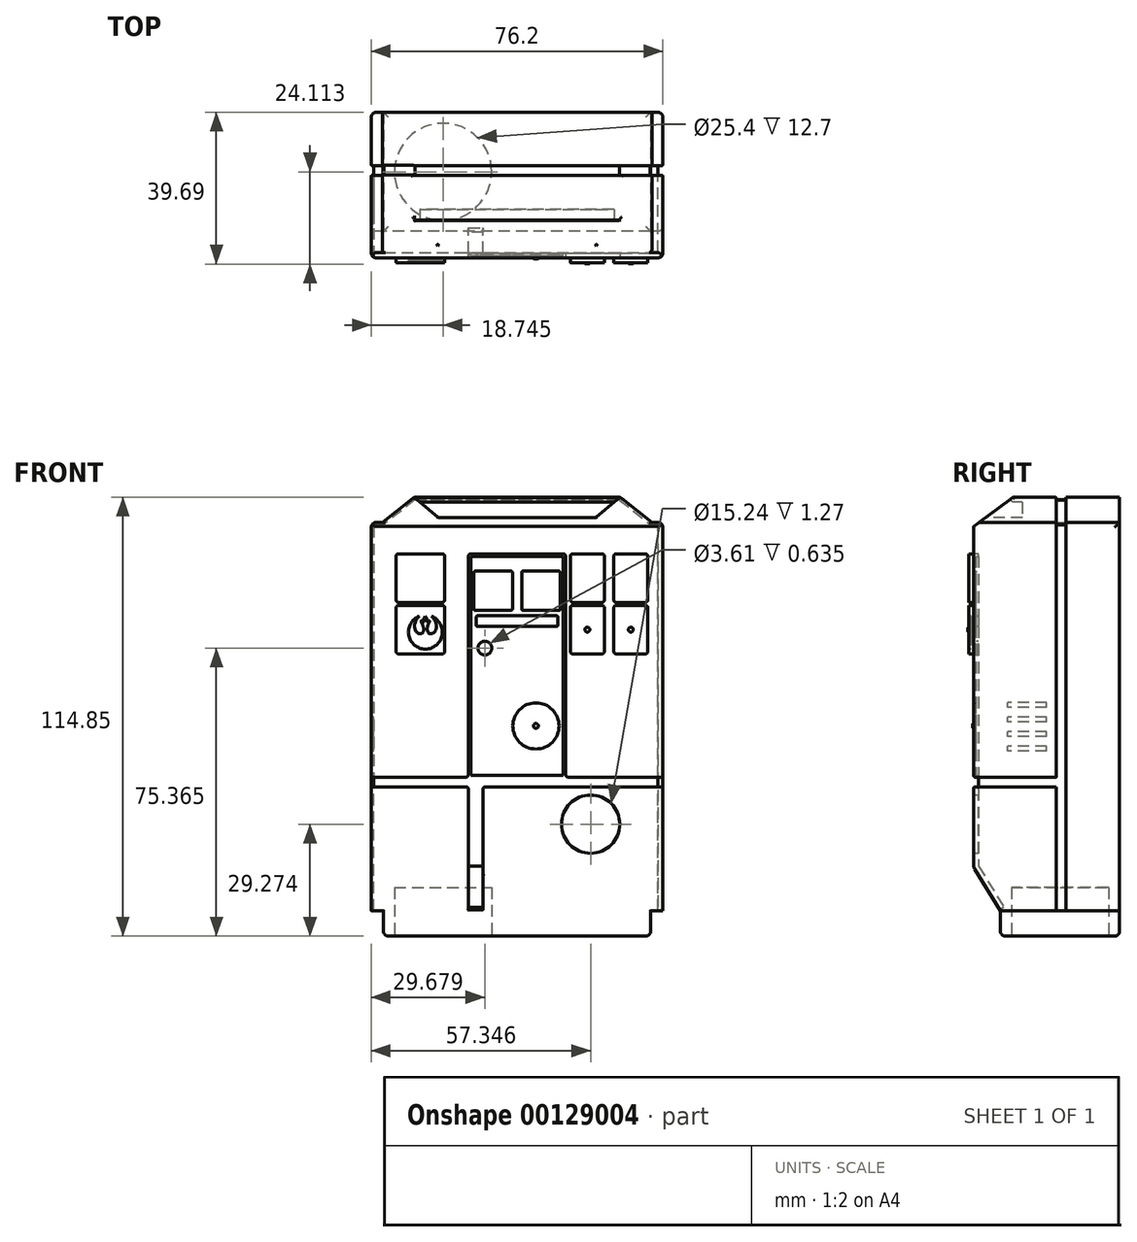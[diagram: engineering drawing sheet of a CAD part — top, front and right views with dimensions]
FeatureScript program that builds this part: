
annotation { "Feature Type Name" : "Feature", "Feature Type Description" : "" }
export const myFeature = defineFeature(function(context is Context, id is Id, definition is map)
    precondition{}
    {
        {
            var Q0;
            Q0=qCreatedBy(makeId("Right.planeOp"),FACE);
            var sketch = newSketch(context, id + "F0", { "sketchPlane" : qUnion([Q0])});
            skLineSegment(sketch, "E0.bottom", {"start": v(19.05, -50.8) * mm, "end": v(-12.1, -50.8) * mm});
            skLineSegment(sketch, "E0.top", {"start": v(19.05, 50.8) * mm, "end": v(-19.05, 50.8) * mm});
            skLineSegment(sketch, "E0.left", {"start": v(19.05, -50.8) * mm, "end": v(19.05, 50.8) * mm});
            skLineSegment(sketch, "E0.right", {"start": v(-19.05, -39.5) * mm, "end": v(-19.05, 50.8) * mm});
            skPoint(sketch, "E0.middle", {"position": v(0, 0) * mm});
            skLineSegment(sketch, "E1", {"start": v(-12.1, -50.8) * mm, "end": v(-19.05, -39.5) * mm});
            skPoint(sketch, "E2.orphan", {"position": v(-19.05, -50.8) * mm});
            skLineSegment(sketch, "E3.bottom", {"start": v(-12.1, -50.8) * mm, "end": v(19.05, -50.8) * mm});
            skLineSegment(sketch, "E3.top", {"start": v(-12.1, -57.41) * mm, "end": v(19.05, -57.41) * mm});
            skLineSegment(sketch, "E3.left", {"start": v(-12.1, -50.8) * mm, "end": v(-12.1, -57.41) * mm});
            skLineSegment(sketch, "E3.right", {"start": v(19.05, -50.8) * mm, "end": v(19.05, -57.41) * mm});
            skLineSegment(sketch, "E4", {"start": v(-44.45, -55.13) * mm, "end": v(6.35, -23.88) * mm, "construction": true});
            skSolve(sketch);
        }
        {
            var Q0;
            Q0=makeQuery(id+"F0.imprint","IMPRINT",FACE,{"disambiguationData":[TD([[makeQuery(id+"F0.imprint","IMPRINT",EDGE,{"derivedFrom":sQuery(id+"F0.wireOp",EDGE,"E0.top")}),1.0]])]});
            extrude(context, id + "F1", {"entities" : qUnion([Q0]), "endBound" : BoundingType.SYMMETRIC, "depth" : 76.2 * mm});
        }
        {
            var Q0;
            Q0 = qSketchRegion(id + "F0", true);
            extrude(context, id + "F2", {"entities" : qUnion([Q0]), "operationType" : NewBodyOperationType.ADD, "endBound" : BoundingType.SYMMETRIC, "depth" : 69.85 * mm});
        }
        {
            var Q0;
            Q0=makeQuery(id+"F1.opExtrude","SWEPT_EDGE",EDGE,{"disambiguationData":[OSD([sQuery(id+"F0.wireOp",EDGE,"E0.right"),sQuery(id+"F0.wireOp",EDGE,"E1")])]});
            var Q1;
            Q1=makeQuery(id+"F1.opExtrude","CAP_EDGE",EDGE,{"disambiguationData":[OSD([sQuery(id+"F0.wireOp",EDGE,"E1")])],"isStart":false});
            var Q2;
            Q2=makeQuery(id+"F1.opExtrude","CAP_EDGE",EDGE,{"disambiguationData":[OSD([sQuery(id+"F0.wireOp",EDGE,"E1")])],"isStart":true});
            var Q3;
            Q3=makeQuery(id+"F1.opExtrude","CAP_EDGE",EDGE,{"disambiguationData":[OSD([sQuery(id+"F0.wireOp",EDGE,"E0.right")])],"isStart":false});
            var Q4;
            Q4=makeQuery(id+"F1.opExtrude","SWEPT_EDGE",EDGE,{"disambiguationData":[OSD([sQuery(id+"F0.wireOp",EDGE,"E0.top"),sQuery(id+"F0.wireOp",EDGE,"E0.right")])]});
            var Q5;
            Q5=makeQuery(id+"F1.opExtrude","CAP_EDGE",EDGE,{"disambiguationData":[OSD([sQuery(id+"F0.wireOp",EDGE,"E0.right")])],"isStart":true});
            var Q6;
            Q6=makeQuery(id+"F1.opExtrude","CAP_EDGE",EDGE,{"disambiguationData":[OSD([sQuery(id+"F0.wireOp",EDGE,"E3.bottom")])],"isStart":true});
            var Q7;
            Q7=makeQuery(id+"F1.opExtrude","CAP_EDGE",EDGE,{"disambiguationData":[OSD([sQuery(id+"F0.wireOp",EDGE,"E3.bottom")])],"isStart":false});
            var Q8;
            Q8=makeQuery(id+"F1.opExtrude","CAP_EDGE",EDGE,{"disambiguationData":[OSD([sQuery(id+"F0.wireOp",EDGE,"E0.top")])],"isStart":false});
            var Q9;
            Q9=makeQuery(id+"F1.opExtrude","CAP_EDGE",EDGE,{"disambiguationData":[OSD([sQuery(id+"F0.wireOp",EDGE,"E0.left")])],"isStart":false});
            var Q10;
            Q10=makeQuery(id+"F1.opExtrude","CAP_EDGE",EDGE,{"disambiguationData":[OSD([sQuery(id+"F0.wireOp",EDGE,"E0.left")])],"isStart":true});
            var Q11;
            Q11=makeQuery(id+"F1.opExtrude","CAP_EDGE",EDGE,{"disambiguationData":[OSD([sQuery(id+"F0.wireOp",EDGE,"E0.top")])],"isStart":true});
            var Q12;
            {var subQ0=sQuery(id+"F0.wireOp",EDGE,"E3.left");var subQ1=sQuery(id+"F0.wireOp",EDGE,"E3.bottom");var subQ2=sQuery(id+"F0.wireOp",EDGE,"E1");Q12=makeQuery(id+"F2.boolean.opBoolean","MERGE",EDGE,{"derivedFrom":[makeQuery(id+"F1.opExtrude","SWEPT_EDGE",EDGE,{"disambiguationData":[OSD([subQ2,subQ1,subQ0])]}),makeQuery(id+"F2.opExtrude","SWEPT_EDGE",EDGE,{"disambiguationData":[OSD([subQ2,subQ1,subQ0])]})]});}
            var Q13;
            Q13=makeQuery(id+"F2.opExtrude","SWEPT_EDGE",EDGE,{"disambiguationData":[OSD([sQuery(id+"F0.wireOp",EDGE,"E3.top"),sQuery(id+"F0.wireOp",EDGE,"E3.left")])]});
            var Q14;
            Q14=makeQuery(id+"F2.opExtrude","CAP_EDGE",EDGE,{"disambiguationData":[OSD([sQuery(id+"F0.wireOp",EDGE,"E3.top")])],"isStart":true});
            var Q15;
            Q15=makeQuery(id+"F2.opExtrude","CAP_EDGE",EDGE,{"disambiguationData":[OSD([sQuery(id+"F0.wireOp",EDGE,"E3.top")])],"isStart":false});
            var Q16;
            Q16=makeQuery(id+"F2.opExtrude","SWEPT_EDGE",EDGE,{"disambiguationData":[OSD([sQuery(id+"F0.wireOp",EDGE,"E3.top"),sQuery(id+"F0.wireOp",EDGE,"E3.right")])]});
            fillet(context, id + "F3", {"entities" : qUnion([Q0, Q1, Q2, Q3, Q4, Q5, Q6, Q7, Q8, Q9, Q10, Q11, Q12, Q13, Q14, Q15, Q16]), "radius" : 1.27 * mm, "tangentPropagation" : true, "allowEdgeOverflow" : false});
        }
        {
            var Q0;
            Q0=makeQuery(id+"F1.opExtrude","SWEPT_FACE",FACE,{"disambiguationData":[OSD([sQuery(id+"F0.wireOp",EDGE,"E0.right")])]});
            var sketch = newSketch(context, id + "F4", { "sketchPlane" : qUnion([Q0])});
            skLineSegment(sketch, "E5.bottom", {"start": v(-31.62, 42.61) * mm, "end": v(-18.92, 42.61) * mm});
            skLineSegment(sketch, "E5.top", {"start": v(-31.62, 29.91) * mm, "end": v(-18.92, 29.91) * mm});
            skLineSegment(sketch, "E5.left", {"start": v(-31.62, 42.61) * mm, "end": v(-31.62, 29.91) * mm});
            skLineSegment(sketch, "E5.right", {"start": v(-18.92, 42.61) * mm, "end": v(-18.92, 29.91) * mm});
            skLineSegment(sketch, "E6.bottom", {"start": v(-31.62, 29.1) * mm, "end": v(-18.92, 29.1) * mm});
            skLineSegment(sketch, "E6.top", {"start": v(-31.62, 16.4) * mm, "end": v(-18.92, 16.4) * mm});
            skLineSegment(sketch, "E6.left", {"start": v(-31.62, 29.1) * mm, "end": v(-31.62, 16.4) * mm});
            skLineSegment(sketch, "E6.right", {"start": v(-18.92, 29.1) * mm, "end": v(-18.92, 16.4) * mm});
            skLineSegment(sketch, "E7.bottom", {"start": v(13.93, 42.61) * mm, "end": v(22.82, 42.61) * mm});
            skLineSegment(sketch, "E7.top", {"start": v(13.93, 29.91) * mm, "end": v(22.82, 29.91) * mm});
            skLineSegment(sketch, "E7.left", {"start": v(13.93, 42.61) * mm, "end": v(13.93, 29.91) * mm});
            skLineSegment(sketch, "E7.right", {"start": v(22.82, 42.61) * mm, "end": v(22.82, 29.91) * mm});
            skLineSegment(sketch, "E8.bottom", {"start": v(13.93, 29.1) * mm, "end": v(22.82, 29.1) * mm});
            skLineSegment(sketch, "E8.top", {"start": v(13.93, 16.4) * mm, "end": v(22.82, 16.4) * mm});
            skLineSegment(sketch, "E8.left", {"start": v(13.93, 29.1) * mm, "end": v(13.93, 16.4) * mm});
            skLineSegment(sketch, "E8.right", {"start": v(22.82, 29.1) * mm, "end": v(22.82, 16.4) * mm});
            skLineSegment(sketch, "E9.bottom", {"start": v(25.3, 42.61) * mm, "end": v(34.19, 42.61) * mm});
            skLineSegment(sketch, "E9.top", {"start": v(25.3, 29.91) * mm, "end": v(34.19, 29.91) * mm});
            skLineSegment(sketch, "E9.left", {"start": v(25.3, 42.61) * mm, "end": v(25.3, 29.91) * mm});
            skLineSegment(sketch, "E9.right", {"start": v(34.19, 42.61) * mm, "end": v(34.19, 29.91) * mm});
            skLineSegment(sketch, "E10.bottom", {"start": v(25.3, 29.1) * mm, "end": v(34.19, 29.1) * mm});
            skLineSegment(sketch, "E10.top", {"start": v(25.3, 16.4) * mm, "end": v(34.19, 16.4) * mm});
            skLineSegment(sketch, "E10.left", {"start": v(25.3, 29.1) * mm, "end": v(25.3, 16.4) * mm});
            skLineSegment(sketch, "E10.right", {"start": v(34.19, 29.1) * mm, "end": v(34.19, 16.4) * mm});
            skSolve(sketch);
        }
        {
            var Q0;
            Q0 = qSketchRegion(id + "F4", true);
            extrude(context, id + "F5", {"entities" : qUnion([Q0]), "operationType" : NewBodyOperationType.ADD, "depth" : 1.27 * mm});
        }
        {
            var Q0;
            Q0=makeQuery(id+"F5.opExtrude","SWEPT_EDGE",EDGE,{"disambiguationData":[OSD([sQuery(id+"F4.wireOp",EDGE,"E5.bottom"),sQuery(id+"F4.wireOp",EDGE,"E5.left")])]});
            var Q1;
            Q1=makeQuery(id+"F5.opExtrude","SWEPT_EDGE",EDGE,{"disambiguationData":[OSD([sQuery(id+"F4.wireOp",EDGE,"E5.top"),sQuery(id+"F4.wireOp",EDGE,"E5.left")])]});
            var Q2;
            Q2=makeQuery(id+"F5.opExtrude","SWEPT_EDGE",EDGE,{"disambiguationData":[OSD([sQuery(id+"F4.wireOp",EDGE,"E6.bottom"),sQuery(id+"F4.wireOp",EDGE,"E6.left")])]});
            var Q3;
            Q3=makeQuery(id+"F5.opExtrude","SWEPT_EDGE",EDGE,{"disambiguationData":[OSD([sQuery(id+"F4.wireOp",EDGE,"E5.top"),sQuery(id+"F4.wireOp",EDGE,"E5.right")])]});
            var Q4;
            Q4=makeQuery(id+"F5.opExtrude","SWEPT_EDGE",EDGE,{"disambiguationData":[OSD([sQuery(id+"F4.wireOp",EDGE,"E6.bottom"),sQuery(id+"F4.wireOp",EDGE,"E6.right")])]});
            var Q5;
            Q5=makeQuery(id+"F5.opExtrude","SWEPT_EDGE",EDGE,{"disambiguationData":[OSD([sQuery(id+"F4.wireOp",EDGE,"E5.bottom"),sQuery(id+"F4.wireOp",EDGE,"E5.right")])]});
            var Q6;
            Q6=makeQuery(id+"F5.opExtrude","SWEPT_EDGE",EDGE,{"disambiguationData":[OSD([sQuery(id+"F4.wireOp",EDGE,"E6.top"),sQuery(id+"F4.wireOp",EDGE,"E6.right")])]});
            var Q7;
            Q7=makeQuery(id+"F5.opExtrude","SWEPT_EDGE",EDGE,{"disambiguationData":[OSD([sQuery(id+"F4.wireOp",EDGE,"E6.top"),sQuery(id+"F4.wireOp",EDGE,"E6.left")])]});
            var Q8;
            Q8=makeQuery(id+"F5.opExtrude","SWEPT_EDGE",EDGE,{"disambiguationData":[OSD([sQuery(id+"F4.wireOp",EDGE,"E8.top"),sQuery(id+"F4.wireOp",EDGE,"E8.left")])]});
            var Q9;
            Q9=makeQuery(id+"F5.opExtrude","SWEPT_EDGE",EDGE,{"disambiguationData":[OSD([sQuery(id+"F4.wireOp",EDGE,"E8.bottom"),sQuery(id+"F4.wireOp",EDGE,"E8.left")])]});
            var Q10;
            Q10=makeQuery(id+"F5.opExtrude","SWEPT_EDGE",EDGE,{"disambiguationData":[OSD([sQuery(id+"F4.wireOp",EDGE,"E7.top"),sQuery(id+"F4.wireOp",EDGE,"E7.left")])]});
            var Q11;
            Q11=makeQuery(id+"F5.opExtrude","SWEPT_EDGE",EDGE,{"disambiguationData":[OSD([sQuery(id+"F4.wireOp",EDGE,"E7.bottom"),sQuery(id+"F4.wireOp",EDGE,"E7.left")])]});
            var Q12;
            Q12=makeQuery(id+"F5.opExtrude","SWEPT_EDGE",EDGE,{"disambiguationData":[OSD([sQuery(id+"F4.wireOp",EDGE,"E8.top"),sQuery(id+"F4.wireOp",EDGE,"E8.right")])]});
            var Q13;
            Q13=makeQuery(id+"F5.opExtrude","SWEPT_EDGE",EDGE,{"disambiguationData":[OSD([sQuery(id+"F4.wireOp",EDGE,"E7.top"),sQuery(id+"F4.wireOp",EDGE,"E7.right")])]});
            var Q14;
            Q14=makeQuery(id+"F5.opExtrude","SWEPT_EDGE",EDGE,{"disambiguationData":[OSD([sQuery(id+"F4.wireOp",EDGE,"E8.bottom"),sQuery(id+"F4.wireOp",EDGE,"E8.right")])]});
            var Q15;
            Q15=makeQuery(id+"F5.opExtrude","SWEPT_EDGE",EDGE,{"disambiguationData":[OSD([sQuery(id+"F4.wireOp",EDGE,"E7.bottom"),sQuery(id+"F4.wireOp",EDGE,"E7.right")])]});
            var Q16;
            Q16=makeQuery(id+"F5.opExtrude","SWEPT_EDGE",EDGE,{"disambiguationData":[OSD([sQuery(id+"F4.wireOp",EDGE,"E10.top"),sQuery(id+"F4.wireOp",EDGE,"E10.right")])]});
            var Q17;
            Q17=makeQuery(id+"F5.opExtrude","SWEPT_EDGE",EDGE,{"disambiguationData":[OSD([sQuery(id+"F4.wireOp",EDGE,"E10.bottom"),sQuery(id+"F4.wireOp",EDGE,"E10.right")])]});
            var Q18;
            Q18=makeQuery(id+"F5.opExtrude","SWEPT_EDGE",EDGE,{"disambiguationData":[OSD([sQuery(id+"F4.wireOp",EDGE,"E9.top"),sQuery(id+"F4.wireOp",EDGE,"E9.right")])]});
            var Q19;
            Q19=makeQuery(id+"F5.opExtrude","SWEPT_EDGE",EDGE,{"disambiguationData":[OSD([sQuery(id+"F4.wireOp",EDGE,"E9.bottom"),sQuery(id+"F4.wireOp",EDGE,"E9.right")])]});
            var Q20;
            Q20=makeQuery(id+"F5.opExtrude","SWEPT_EDGE",EDGE,{"disambiguationData":[OSD([sQuery(id+"F4.wireOp",EDGE,"E10.top"),sQuery(id+"F4.wireOp",EDGE,"E10.left")])]});
            var Q21;
            Q21=makeQuery(id+"F5.opExtrude","SWEPT_EDGE",EDGE,{"disambiguationData":[OSD([sQuery(id+"F4.wireOp",EDGE,"E10.bottom"),sQuery(id+"F4.wireOp",EDGE,"E10.left")])]});
            var Q22;
            Q22=makeQuery(id+"F5.opExtrude","SWEPT_EDGE",EDGE,{"disambiguationData":[OSD([sQuery(id+"F4.wireOp",EDGE,"E9.top"),sQuery(id+"F4.wireOp",EDGE,"E9.left")])]});
            var Q23;
            Q23=makeQuery(id+"F5.opExtrude","SWEPT_EDGE",EDGE,{"disambiguationData":[OSD([sQuery(id+"F4.wireOp",EDGE,"E9.bottom"),sQuery(id+"F4.wireOp",EDGE,"E9.left")])]});
            fillet(context, id + "F6", {"entities" : qUnion([Q0, Q1, Q2, Q3, Q4, Q5, Q6, Q7, Q8, Q9, Q10, Q11, Q12, Q13, Q14, Q15, Q16, Q17, Q18, Q19, Q20, Q21, Q22, Q23]), "radius" : 0.64 * mm, "tangentPropagation" : true, "allowEdgeOverflow" : false});
        }
        {
            var Q0;
            Q0=makeQuery(id+"F1.opExtrude","SWEPT_FACE",FACE,{"disambiguationData":[OSD([sQuery(id+"F0.wireOp",EDGE,"E0.right")])]});
            var sketch = newSketch(context, id + "F7", { "sketchPlane" : qUnion([Q0])});
            skLineSegment(sketch, "E11.bottom", {"start": v(-12.7, 42.61) * mm, "end": v(12.7, 42.61) * mm});
            skLineSegment(sketch, "E11.left", {"start": v(-12.7, 42.61) * mm, "end": v(-12.7, -15.8) * mm});
            skLineSegment(sketch, "E11.right", {"start": v(12.7, 42.61) * mm, "end": v(12.7, -15.8) * mm});
            skLineSegment(sketch, "E12.bottom", {"start": v(-36.83, -15.8) * mm, "end": v(-12.7, -15.8) * mm});
            skLineSegment(sketch, "E12.top", {"start": v(-36.83, -18.35) * mm, "end": v(-12.7, -18.35) * mm});
            skLineSegment(sketch, "E12.left", {"start": v(-38.72, -15.8) * mm, "end": v(-38.72, -18.35) * mm});
            skLineSegment(sketch, "E12.right", {"start": v(36.83, -15.8) * mm, "end": v(36.83, -18.35) * mm});
            skLineSegment(sketch, "E13.top", {"start": v(-12.7, -39.14) * mm, "end": v(-8.9, -39.14) * mm});
            skLineSegment(sketch, "E13.left", {"start": v(-12.7, -18.35) * mm, "end": v(-12.7, -39.14) * mm});
            skLineSegment(sketch, "E13.right", {"start": v(-8.9, -18.35) * mm, "end": v(-8.9, -39.14) * mm});
            skLineSegment(sketch, "E14.trimOffspring", {"start": v(12.7, -15.8) * mm, "end": v(36.83, -15.8) * mm});
            skLineSegment(sketch, "E15.trimOffspring", {"start": v(-8.9, -18.35) * mm, "end": v(36.83, -18.35) * mm});
            skLineSegment(sketch, "E16", {"start": v(-36.83, -15.8) * mm, "end": v(-38.72, -15.8) * mm});
            skLineSegment(sketch, "E17", {"start": v(-38.72, -18.35) * mm, "end": v(-36.83, -18.35) * mm});
            skLineSegment(sketch, "E18", {"start": v(36.83, -15.8) * mm, "end": v(39.7, -15.8) * mm});
            skLineSegment(sketch, "E19", {"start": v(39.7, -15.8) * mm, "end": v(39.7, -18.35) * mm});
            skLineSegment(sketch, "E20", {"start": v(39.7, -18.35) * mm, "end": v(36.83, -18.35) * mm});
            skLineSegment(sketch, "E21", {"start": v(-12.7, -39.14) * mm, "end": v(-12.7, -46.52) * mm});
            skLineSegment(sketch, "E22", {"start": v(-12.7, -46.52) * mm, "end": v(-8.9, -46.52) * mm});
            skLineSegment(sketch, "E23", {"start": v(-8.9, -46.52) * mm, "end": v(-8.9, -39.14) * mm});
            skCircle(sketch, "E24", {"center": v(19.25, -28.14) * mm, "radius": 7.62 * mm});
            skSolve(sketch);
        }
        {
            var Q0;
            Q0 = qSketchRegion(id + "F7", true);
            extrude(context, id + "F8", {"entities" : qUnion([Q0]), "operationType" : NewBodyOperationType.REMOVE, "oppositeDirection" : true, "depth" : 1.27 * mm});
        }
        {
            var Q0;
            Q0=makeQuery(id+"F8.boolean.opBoolean","COPY",EDGE,{"derivedFrom":makeQuery(id+"F8.opExtrude","SWEPT_EDGE",EDGE,{"disambiguationData":[OSD([sQuery(id+"F7.wireOp",EDGE,"E12.top"),sQuery(id+"F7.wireOp",EDGE,"E13.left")])]})});
            var Q1;
            Q1=makeQuery(id+"F8.boolean.opBoolean","COPY",EDGE,{"derivedFrom":makeQuery(id+"F8.opExtrude","SWEPT_EDGE",EDGE,{"disambiguationData":[OSD([sQuery(id+"F7.wireOp",EDGE,"E11.left"),sQuery(id+"F7.wireOp",EDGE,"E12.bottom")])]})});
            var Q2;
            Q2=makeQuery(id+"F8.boolean.opBoolean","COPY",EDGE,{"derivedFrom":makeQuery(id+"F8.opExtrude","SWEPT_EDGE",EDGE,{"disambiguationData":[OSD([sQuery(id+"F7.wireOp",EDGE,"E13.right"),sQuery(id+"F7.wireOp",EDGE,"E15.trimOffspring")])]})});
            var Q3;
            Q3=makeQuery(id+"F8.boolean.opBoolean","COPY",EDGE,{"derivedFrom":makeQuery(id+"F8.opExtrude","SWEPT_EDGE",EDGE,{"disambiguationData":[OSD([sQuery(id+"F7.wireOp",EDGE,"E11.right"),sQuery(id+"F7.wireOp",EDGE,"E14.trimOffspring")])]})});
            var Q4;
            Q4=makeQuery(id+"F8.boolean.opBoolean","COPY",EDGE,{"derivedFrom":makeQuery(id+"F8.opExtrude","SWEPT_EDGE",EDGE,{"disambiguationData":[OSD([sQuery(id+"F7.wireOp",EDGE,"E11.bottom"),sQuery(id+"F7.wireOp",EDGE,"E11.left")])]})});
            var Q5;
            Q5=makeQuery(id+"F8.boolean.opBoolean","COPY",EDGE,{"derivedFrom":makeQuery(id+"F8.opExtrude","SWEPT_EDGE",EDGE,{"disambiguationData":[OSD([sQuery(id+"F7.wireOp",EDGE,"E11.bottom"),sQuery(id+"F7.wireOp",EDGE,"E11.right")])]})});
            fillet(context, id + "F9", {"entities" : qUnion([Q0, Q1, Q2, Q3, Q4, Q5]), "radius" : 0.64 * mm, "tangentPropagation" : true, "allowEdgeOverflow" : false});
        }
        {
            var Q0;
            Q0=makeQuery(id+"F8.boolean.opBoolean","COPY",EDGE,{"derivedFrom":makeQuery(id+"F8.opExtrude","CAP_EDGE",EDGE,{"disambiguationData":[OSD([sQuery(id+"F7.wireOp",EDGE,"E11.left")])],"isStart":true})});
            var Q1;
            Q1=makeQuery(id+"F8.boolean.opBoolean","COPY",EDGE,{"derivedFrom":makeQuery(id+"F8.opExtrude","CAP_EDGE",EDGE,{"disambiguationData":[OSD([sQuery(id+"F7.wireOp",EDGE,"E11.bottom")])],"isStart":true})});
            var Q2;
            {var subQ13=sQuery(id+"F0.wireOp",EDGE,"E0.right");var subQ16=sQuery(id+"F4.wireOp",EDGE,"E5.bottom");var subQ26=sQuery(id+"F7.wireOp",EDGE,"E11.bottom");var subQ27=sQuery(id+"F7.wireOp",EDGE,"E11.right");Q2=makeQuery(id+"F9.opFillet","BLEND_EDGE",EDGE,{"blendedFrom":[makeQuery(id+"F8.boolean.opBoolean","COPY",EDGE,{"derivedFrom":makeQuery(id+"F8.opExtrude","SWEPT_EDGE",EDGE,{"disambiguationData":[OSD([subQ26,subQ27])]})}),makeQuery(id+"F8.boolean.opBoolean","SPLIT",FACE,{"disambiguationData":[TD([makeQuery(id+"F5.opExtrude","SWEPT_FACE",FACE,{"disambiguationData":[OSD([subQ16])]})])],"derivedFrom":makeQuery(id+"F1.opExtrude","SWEPT_FACE",FACE,{"disambiguationData":[OSD([subQ13])]})})],"blendedInto":[makeQuery(id+"F8.boolean.opBoolean","SPLIT",FACE,{"disambiguationData":[TD([makeQuery(id+"F5.opExtrude","SWEPT_FACE",FACE,{"disambiguationData":[OSD([subQ16])]})])],"derivedFrom":makeQuery(id+"F1.opExtrude","SWEPT_FACE",FACE,{"disambiguationData":[OSD([subQ13])]})})]});}
            var Q3;
            Q3=makeQuery(id+"F8.boolean.opBoolean","COPY",EDGE,{"derivedFrom":makeQuery(id+"F8.opExtrude","CAP_EDGE",EDGE,{"disambiguationData":[OSD([sQuery(id+"F7.wireOp",EDGE,"E11.right")])],"isStart":true})});
            var Q4;
            {var subQ13=sQuery(id+"F0.wireOp",EDGE,"E0.right");var subQ16=sQuery(id+"F4.wireOp",EDGE,"E5.bottom");var subQ26=sQuery(id+"F7.wireOp",EDGE,"E11.bottom");var subQ27=sQuery(id+"F7.wireOp",EDGE,"E11.left");Q4=makeQuery(id+"F9.opFillet","BLEND_EDGE",EDGE,{"blendedFrom":[makeQuery(id+"F8.boolean.opBoolean","COPY",EDGE,{"derivedFrom":makeQuery(id+"F8.opExtrude","SWEPT_EDGE",EDGE,{"disambiguationData":[OSD([subQ26,subQ27])]})}),makeQuery(id+"F8.boolean.opBoolean","SPLIT",FACE,{"disambiguationData":[TD([makeQuery(id+"F5.opExtrude","SWEPT_FACE",FACE,{"disambiguationData":[OSD([subQ16])]})])],"derivedFrom":makeQuery(id+"F1.opExtrude","SWEPT_FACE",FACE,{"disambiguationData":[OSD([subQ13])]})})],"blendedInto":[makeQuery(id+"F8.boolean.opBoolean","SPLIT",FACE,{"disambiguationData":[TD([makeQuery(id+"F5.opExtrude","SWEPT_FACE",FACE,{"disambiguationData":[OSD([subQ16])]})])],"derivedFrom":makeQuery(id+"F1.opExtrude","SWEPT_FACE",FACE,{"disambiguationData":[OSD([subQ13])]})})]});}
            var Q5;
            Q5=makeQuery(id+"F8.boolean.opBoolean","COPY",EDGE,{"derivedFrom":makeQuery(id+"F8.opExtrude","CAP_EDGE",EDGE,{"disambiguationData":[OSD([sQuery(id+"F7.wireOp",EDGE,"E12.bottom"),sQuery(id+"F7.wireOp",EDGE,"E16")])],"isStart":true})});
            var Q6;
            Q6=makeQuery(id+"F8.boolean.opBoolean","COPY",EDGE,{"derivedFrom":makeQuery(id+"F8.opExtrude","CAP_EDGE",EDGE,{"disambiguationData":[OSD([sQuery(id+"F7.wireOp",EDGE,"E12.top"),sQuery(id+"F7.wireOp",EDGE,"E17")])],"isStart":true})});
            var Q7;
            {var subQ0=sQuery(id+"F0.wireOp",EDGE,"E0.right");Q7=makeQuery(id+"F8.boolean.opBoolean","INTERSECT",EDGE,{"derivedFrom":[makeQuery(id+"F3.opFillet","BLEND_FACE",FACE,{"disambiguationData":[OSD([subQ0]),TDD([makeQuery(id+"F1.opExtrude","CAP_EDGE",EDGE,{"disambiguationData":[OSD([subQ0])],"isStart":true})])]}),makeQuery(id+"F8.opExtrude","SWEPT_FACE",FACE,{"disambiguationData":[OSD([sQuery(id+"F7.wireOp",EDGE,"E12.bottom"),sQuery(id+"F7.wireOp",EDGE,"E16")])]})]});}
            var Q8;
            {var subQ0=sQuery(id+"F0.wireOp",EDGE,"E0.right");Q8=makeQuery(id+"F8.boolean.opBoolean","INTERSECT",EDGE,{"derivedFrom":[makeQuery(id+"F3.opFillet","BLEND_FACE",FACE,{"disambiguationData":[OSD([subQ0]),TDD([makeQuery(id+"F1.opExtrude","CAP_EDGE",EDGE,{"disambiguationData":[OSD([subQ0])],"isStart":true})])]}),makeQuery(id+"F8.opExtrude","SWEPT_FACE",FACE,{"disambiguationData":[OSD([sQuery(id+"F7.wireOp",EDGE,"E12.top"),sQuery(id+"F7.wireOp",EDGE,"E17")])]})]});}
            var Q9;
            {var subQ13=sQuery(id+"F0.wireOp",EDGE,"E0.right");var subQ16=sQuery(id+"F4.wireOp",EDGE,"E5.bottom");var subQ26=sQuery(id+"F7.wireOp",EDGE,"E11.left");var subQ27=sQuery(id+"F7.wireOp",EDGE,"E12.bottom");Q9=makeQuery(id+"F9.opFillet","BLEND_EDGE",EDGE,{"blendedFrom":[makeQuery(id+"F8.boolean.opBoolean","COPY",EDGE,{"derivedFrom":makeQuery(id+"F8.opExtrude","SWEPT_EDGE",EDGE,{"disambiguationData":[OSD([subQ26,subQ27])]})}),makeQuery(id+"F8.boolean.opBoolean","SPLIT",FACE,{"disambiguationData":[TD([makeQuery(id+"F5.opExtrude","SWEPT_FACE",FACE,{"disambiguationData":[OSD([subQ16])]})])],"derivedFrom":makeQuery(id+"F1.opExtrude","SWEPT_FACE",FACE,{"disambiguationData":[OSD([subQ13])]})})],"blendedInto":[makeQuery(id+"F8.boolean.opBoolean","SPLIT",FACE,{"disambiguationData":[TD([makeQuery(id+"F5.opExtrude","SWEPT_FACE",FACE,{"disambiguationData":[OSD([subQ16])]})])],"derivedFrom":makeQuery(id+"F1.opExtrude","SWEPT_FACE",FACE,{"disambiguationData":[OSD([subQ13])]})})]});}
            var Q10;
            {var subQ0=sQuery(id+"F7.wireOp",EDGE,"E12.top");var subQ2=sQuery(id+"F0.wireOp",EDGE,"E0.right");var subQ3=sQuery(id+"F7.wireOp",EDGE,"E13.left");Q10=makeQuery(id+"F9.opFillet","BLEND_EDGE",EDGE,{"blendedFrom":[makeQuery(id+"F8.boolean.opBoolean","COPY",EDGE,{"derivedFrom":makeQuery(id+"F8.opExtrude","SWEPT_EDGE",EDGE,{"disambiguationData":[OSD([subQ0,subQ3])]})}),makeQuery(id+"F8.boolean.opBoolean","SPLIT",FACE,{"disambiguationData":[TD([makeQuery(id+"F8.opExtrude","SWEPT_FACE",FACE,{"disambiguationData":[OSD([subQ0,sQuery(id+"F7.wireOp",EDGE,"E17")])]})])],"derivedFrom":makeQuery(id+"F1.opExtrude","SWEPT_FACE",FACE,{"disambiguationData":[OSD([subQ2])]})})],"blendedInto":[makeQuery(id+"F8.boolean.opBoolean","SPLIT",FACE,{"disambiguationData":[TD([makeQuery(id+"F8.opExtrude","SWEPT_FACE",FACE,{"disambiguationData":[OSD([subQ0,sQuery(id+"F7.wireOp",EDGE,"E17")])]})])],"derivedFrom":makeQuery(id+"F1.opExtrude","SWEPT_FACE",FACE,{"disambiguationData":[OSD([subQ2])]})})]});}
            var Q11;
            Q11=makeQuery(id+"F8.boolean.opBoolean","COPY",EDGE,{"derivedFrom":makeQuery(id+"F8.opExtrude","CAP_EDGE",EDGE,{"disambiguationData":[OSD([sQuery(id+"F7.wireOp",EDGE,"E13.left"),sQuery(id+"F7.wireOp",EDGE,"E21")])],"isStart":true})});
            var Q12;
            Q12=makeQuery(id+"F8.boolean.opBoolean","COPY",EDGE,{"derivedFrom":makeQuery(id+"F8.opExtrude","CAP_EDGE",EDGE,{"disambiguationData":[OSD([sQuery(id+"F7.wireOp",EDGE,"E13.right"),sQuery(id+"F7.wireOp",EDGE,"E23")])],"isStart":true})});
            var Q13;
            {var subQ1=sQuery(id+"F0.wireOp",EDGE,"E0.right");var subQ2=sQuery(id+"F7.wireOp",EDGE,"E13.right");var subQ3=sQuery(id+"F7.wireOp",EDGE,"E15.trimOffspring");Q13=makeQuery(id+"F9.opFillet","BLEND_EDGE",EDGE,{"blendedFrom":[makeQuery(id+"F8.boolean.opBoolean","COPY",EDGE,{"derivedFrom":makeQuery(id+"F8.opExtrude","SWEPT_EDGE",EDGE,{"disambiguationData":[OSD([subQ2,subQ3])]})}),makeQuery(id+"F8.boolean.opBoolean","SPLIT",FACE,{"disambiguationData":[TD([makeQuery(id+"F8.opExtrude","SWEPT_FACE",FACE,{"disambiguationData":[OSD([subQ2,sQuery(id+"F7.wireOp",EDGE,"E23")])]})])],"derivedFrom":makeQuery(id+"F1.opExtrude","SWEPT_FACE",FACE,{"disambiguationData":[OSD([subQ1])]})})],"blendedInto":[makeQuery(id+"F8.boolean.opBoolean","SPLIT",FACE,{"disambiguationData":[TD([makeQuery(id+"F8.opExtrude","SWEPT_FACE",FACE,{"disambiguationData":[OSD([subQ2,sQuery(id+"F7.wireOp",EDGE,"E23")])]})])],"derivedFrom":makeQuery(id+"F1.opExtrude","SWEPT_FACE",FACE,{"disambiguationData":[OSD([subQ1])]})})]});}
            var Q14;
            Q14=makeQuery(id+"F8.boolean.opBoolean","COPY",EDGE,{"derivedFrom":makeQuery(id+"F8.opExtrude","CAP_EDGE",EDGE,{"disambiguationData":[OSD([sQuery(id+"F7.wireOp",EDGE,"E15.trimOffspring"),sQuery(id+"F7.wireOp",EDGE,"E20")])],"isStart":true})});
            var Q15;
            {var subQ13=sQuery(id+"F0.wireOp",EDGE,"E0.right");var subQ16=sQuery(id+"F4.wireOp",EDGE,"E5.bottom");var subQ26=sQuery(id+"F7.wireOp",EDGE,"E11.right");var subQ27=sQuery(id+"F7.wireOp",EDGE,"E14.trimOffspring");Q15=makeQuery(id+"F9.opFillet","BLEND_EDGE",EDGE,{"blendedFrom":[makeQuery(id+"F8.boolean.opBoolean","COPY",EDGE,{"derivedFrom":makeQuery(id+"F8.opExtrude","SWEPT_EDGE",EDGE,{"disambiguationData":[OSD([subQ26,subQ27])]})}),makeQuery(id+"F8.boolean.opBoolean","SPLIT",FACE,{"disambiguationData":[TD([makeQuery(id+"F5.opExtrude","SWEPT_FACE",FACE,{"disambiguationData":[OSD([subQ16])]})])],"derivedFrom":makeQuery(id+"F1.opExtrude","SWEPT_FACE",FACE,{"disambiguationData":[OSD([subQ13])]})})],"blendedInto":[makeQuery(id+"F8.boolean.opBoolean","SPLIT",FACE,{"disambiguationData":[TD([makeQuery(id+"F5.opExtrude","SWEPT_FACE",FACE,{"disambiguationData":[OSD([subQ16])]})])],"derivedFrom":makeQuery(id+"F1.opExtrude","SWEPT_FACE",FACE,{"disambiguationData":[OSD([subQ13])]})})]});}
            var Q16;
            Q16=makeQuery(id+"F8.boolean.opBoolean","COPY",EDGE,{"derivedFrom":makeQuery(id+"F8.opExtrude","CAP_EDGE",EDGE,{"disambiguationData":[OSD([sQuery(id+"F7.wireOp",EDGE,"E14.trimOffspring"),sQuery(id+"F7.wireOp",EDGE,"E18")])],"isStart":true})});
            var Q17;
            {var subQ0=sQuery(id+"F0.wireOp",EDGE,"E0.right");Q17=makeQuery(id+"F8.boolean.opBoolean","INTERSECT",EDGE,{"derivedFrom":[makeQuery(id+"F3.opFillet","BLEND_FACE",FACE,{"disambiguationData":[OSD([subQ0]),TDD([makeQuery(id+"F1.opExtrude","CAP_EDGE",EDGE,{"disambiguationData":[OSD([subQ0])],"isStart":false})])]}),makeQuery(id+"F8.opExtrude","SWEPT_FACE",FACE,{"disambiguationData":[OSD([sQuery(id+"F7.wireOp",EDGE,"E15.trimOffspring"),sQuery(id+"F7.wireOp",EDGE,"E20")])]})]});}
            var Q18;
            {var subQ0=sQuery(id+"F0.wireOp",EDGE,"E0.right");Q18=makeQuery(id+"F8.boolean.opBoolean","INTERSECT",EDGE,{"derivedFrom":[makeQuery(id+"F3.opFillet","BLEND_FACE",FACE,{"disambiguationData":[OSD([subQ0]),TDD([makeQuery(id+"F1.opExtrude","CAP_EDGE",EDGE,{"disambiguationData":[OSD([subQ0])],"isStart":false})])]}),makeQuery(id+"F8.opExtrude","SWEPT_FACE",FACE,{"disambiguationData":[OSD([sQuery(id+"F7.wireOp",EDGE,"E14.trimOffspring"),sQuery(id+"F7.wireOp",EDGE,"E18")])]})]});}
            fillet(context, id + "F10", {"entities" : qUnion([Q0, Q1, Q2, Q3, Q4, Q5, Q6, Q7, Q8, Q9, Q10, Q11, Q12, Q13, Q14, Q15, Q16, Q17, Q18]), "radius" : 0.32 * mm, "tangentPropagation" : true, "allowEdgeOverflow" : false});
        }
        {
            var Q0;
            Q0=sQuery(id+"F0.wireOp",EDGE,"E4");
            cPlane(context, id + "F11", {"entities" : qUnion([Q0]), "cplaneType" : CPlaneType.MID_PLANE, "offset" : 25.4 * mm, "width" : 152.4 * mm, "height" : 152.4 * mm});
        }
        {
            var Q0;
            Q0=qCreatedBy(id+"F11.planeOp",FACE);
            var sketch = newSketch(context, id + "F12", { "sketchPlane" : qUnion([Q0])});
            skLineSegment(sketch, "E25.bottom", {"start": v(12.7, -23.99) * mm, "end": v(8.89, -23.99) * mm});
            skLineSegment(sketch, "E25.top", {"start": v(12.7, -36.6) * mm, "end": v(8.89, -36.6) * mm});
            skLineSegment(sketch, "E25.left", {"start": v(12.7, -23.99) * mm, "end": v(12.7, -36.6) * mm});
            skLineSegment(sketch, "E25.right", {"start": v(8.89, -23.99) * mm, "end": v(8.89, -36.6) * mm});
            skSolve(sketch);
        }
        {
            var Q0;
            Q0 = qSketchRegion(id + "F12", true);
            extrude(context, id + "F13", {"entities" : qUnion([Q0]), "operationType" : NewBodyOperationType.REMOVE, "depth" : 1.27 * mm});
        }
        {
            var Q0;
            Q0=makeQuery(id+"F13.boolean.opBoolean","COPY",EDGE,{"disambiguationData":[OD(1.0)],"derivedFrom":makeQuery(id+"F13.opExtrude","CAP_EDGE",EDGE,{"disambiguationData":[OSD([sQuery(id+"F12.wireOp",EDGE,"E25.left")])],"isStart":true})});
            var Q1;
            Q1=makeQuery(id+"F13.boolean.opBoolean","COPY",EDGE,{"disambiguationData":[OD(1.0)],"derivedFrom":makeQuery(id+"F13.opExtrude","CAP_EDGE",EDGE,{"disambiguationData":[OSD([sQuery(id+"F12.wireOp",EDGE,"E25.right")])],"isStart":true})});
            fillet(context, id + "F14", {"entities" : qUnion([Q0, Q1]), "radius" : 0.32 * mm, "tangentPropagation" : true, "allowEdgeOverflow" : false});
        }
        {
            var Q0;
            {var subQ0=sQuery(id+"F7.wireOp",EDGE,"E17");var subQ1=sQuery(id+"F7.wireOp",EDGE,"E12.top");var subQ3=sQuery(id+"F7.wireOp",EDGE,"E13.left");var subQ4=sQuery(id+"F7.wireOp",EDGE,"E11.right");var subQ5=sQuery(id+"F7.wireOp",EDGE,"E11.bottom");var subQ6=sQuery(id+"F7.wireOp",EDGE,"E11.left");var subQ7=sQuery(id+"F7.wireOp",EDGE,"E14.trimOffspring");var subQ8=sQuery(id+"F7.wireOp",EDGE,"E20");var subQ9=sQuery(id+"F7.wireOp",EDGE,"E15.trimOffspring");var subQ10=sQuery(id+"F7.wireOp",EDGE,"E18");var subQ11=sQuery(id+"F7.wireOp",EDGE,"E23");var subQ12=sQuery(id+"F7.wireOp",EDGE,"E13.right");var subQ17=sQuery(id+"F7.wireOp",EDGE,"E16");var subQ18=sQuery(id+"F7.wireOp",EDGE,"E12.bottom");var subQ19=sQuery(id+"F7.wireOp",EDGE,"E21");Q0=makeQuery(id+"F13.boolean.opBoolean","SPLIT",FACE,{"disambiguationData":[TD([makeQuery(id+"F8.boolean.opBoolean","COPY",FACE,{"derivedFrom":makeQuery(id+"F8.opExtrude","SWEPT_FACE",FACE,{"disambiguationData":[OSD([subQ5])]})})])],"derivedFrom":makeQuery(id+"F8.boolean.opBoolean","COPY",FACE,{"derivedFrom":makeQuery(id+"F8.opExtrude","CAP_FACE",FACE,{"disambiguationData":[OSD([subQ5,subQ6,subQ4,subQ18,subQ1,sQuery(id+"F7.wireOp",EDGE,"E12.left"),subQ3,subQ12,subQ7,subQ9,subQ17,subQ0,subQ10,sQuery(id+"F7.wireOp",EDGE,"E19"),subQ8,subQ19,sQuery(id+"F7.wireOp",EDGE,"E22"),subQ11])],"isStart":false})})});}
            var sketch = newSketch(context, id + "F15", { "sketchPlane" : qUnion([Q0])});
            skCircle(sketch, "E26", {"center": v(4.93, -2.43) * mm, "radius": 6.04 * mm});
            skLineSegment(sketch, "E27.bottom", {"start": v(-1.22, 27.81) * mm, "end": v(-11.27, 27.81) * mm});
            skLineSegment(sketch, "E27.top", {"start": v(-1.22, 38.06) * mm, "end": v(-11.27, 38.06) * mm});
            skLineSegment(sketch, "E27.left", {"start": v(-1.22, 27.81) * mm, "end": v(-1.22, 38.06) * mm});
            skLineSegment(sketch, "E27.right", {"start": v(-11.27, 27.81) * mm, "end": v(-11.27, 38.06) * mm});
            skPoint(sketch, "E27.middle", {"position": v(-6.24, 32.94) * mm});
            skLineSegment(sketch, "E28.MirrorCS", {"start": v(1.22, 27.81) * mm, "end": v(1.22, 38.06) * mm});
            skLineSegment(sketch, "E29.MirrorCS", {"start": v(1.22, 27.81) * mm, "end": v(11.27, 27.81) * mm});
            skLineSegment(sketch, "E30.MirrorCS", {"start": v(1.22, 38.06) * mm, "end": v(11.27, 38.06) * mm});
            skLineSegment(sketch, "E31.MirrorCS", {"start": v(11.27, 27.81) * mm, "end": v(11.27, 38.06) * mm});
            skPoint(sketch, "E32.MirrorP", {"position": v(6.24, 32.94) * mm});
            skLineSegment(sketch, "E33.bottom", {"start": v(-12.07, 41.98) * mm, "end": v(12.06, 41.98) * mm});
            skLineSegment(sketch, "E33.top", {"start": v(-12.07, -15.37) * mm, "end": v(12.06, -15.37) * mm});
            skLineSegment(sketch, "E33.left", {"start": v(-12.07, 41.98) * mm, "end": v(-12.07, -15.37) * mm});
            skLineSegment(sketch, "E33.right", {"start": v(12.06, 41.98) * mm, "end": v(12.06, -15.37) * mm});
            skLineSegment(sketch, "E34.bottom", {"start": v(-10.67, 26.38) * mm, "end": v(10.67, 26.38) * mm});
            skLineSegment(sketch, "E34.top", {"start": v(-10.67, 23.62) * mm, "end": v(10.67, 23.62) * mm});
            skLineSegment(sketch, "E34.left", {"start": v(-10.67, 26.38) * mm, "end": v(-10.67, 23.62) * mm});
            skLineSegment(sketch, "E34.right", {"start": v(10.67, 26.38) * mm, "end": v(10.67, 23.62) * mm});
            skCircle(sketch, "E35", {"center": v(-8.42, 17.95) * mm, "radius": 1.8 * mm});
            skSolve(sketch);
        }
        {
            var Q0;
            Q0 = qSketchRegion(id + "F15", true);
            extrude(context, id + "F16", {"entities" : qUnion([Q0]), "operationType" : NewBodyOperationType.ADD, "depth" : 0.64 * mm});
        }
        {
            var Q0;
            {var subQ0=sQuery(id+"F7.wireOp",EDGE,"E17");var subQ1=sQuery(id+"F7.wireOp",EDGE,"E12.top");var subQ3=sQuery(id+"F7.wireOp",EDGE,"E13.left");var subQ4=sQuery(id+"F7.wireOp",EDGE,"E11.right");var subQ5=sQuery(id+"F7.wireOp",EDGE,"E11.bottom");var subQ6=sQuery(id+"F7.wireOp",EDGE,"E11.left");var subQ7=sQuery(id+"F7.wireOp",EDGE,"E14.trimOffspring");var subQ8=sQuery(id+"F7.wireOp",EDGE,"E20");var subQ9=sQuery(id+"F7.wireOp",EDGE,"E15.trimOffspring");var subQ10=sQuery(id+"F7.wireOp",EDGE,"E18");var subQ11=sQuery(id+"F7.wireOp",EDGE,"E23");var subQ12=sQuery(id+"F7.wireOp",EDGE,"E13.right");var subQ17=sQuery(id+"F7.wireOp",EDGE,"E16");var subQ18=sQuery(id+"F7.wireOp",EDGE,"E12.bottom");var subQ19=sQuery(id+"F7.wireOp",EDGE,"E21");Q0=makeQuery(id+"F16.boolean.opBoolean","SPLIT",FACE,{"disambiguationData":[TD([makeQuery(id+"F16.opExtrude","SWEPT_FACE",FACE,{"disambiguationData":[OSD([sQuery(id+"F15.wireOp",EDGE,"E27.bottom")])]})])],"derivedFrom":makeQuery(id+"F13.boolean.opBoolean","SPLIT",FACE,{"disambiguationData":[TD([makeQuery(id+"F8.boolean.opBoolean","COPY",FACE,{"derivedFrom":makeQuery(id+"F8.opExtrude","SWEPT_FACE",FACE,{"disambiguationData":[OSD([subQ5])]})})])],"derivedFrom":makeQuery(id+"F8.boolean.opBoolean","COPY",FACE,{"derivedFrom":makeQuery(id+"F8.opExtrude","CAP_FACE",FACE,{"disambiguationData":[OSD([subQ5,subQ6,subQ4,subQ18,subQ1,sQuery(id+"F7.wireOp",EDGE,"E12.left"),subQ3,subQ12,subQ7,subQ9,subQ17,subQ0,subQ10,sQuery(id+"F7.wireOp",EDGE,"E19"),subQ8,subQ19,sQuery(id+"F7.wireOp",EDGE,"E22"),subQ11])],"isStart":false})})})});}
            var Q1;
            {var subQ0=sQuery(id+"F7.wireOp",EDGE,"E17");var subQ1=sQuery(id+"F7.wireOp",EDGE,"E12.top");var subQ3=sQuery(id+"F7.wireOp",EDGE,"E13.left");var subQ4=sQuery(id+"F7.wireOp",EDGE,"E11.right");var subQ5=sQuery(id+"F7.wireOp",EDGE,"E11.bottom");var subQ6=sQuery(id+"F7.wireOp",EDGE,"E11.left");var subQ7=sQuery(id+"F7.wireOp",EDGE,"E14.trimOffspring");var subQ8=sQuery(id+"F7.wireOp",EDGE,"E20");var subQ9=sQuery(id+"F7.wireOp",EDGE,"E15.trimOffspring");var subQ10=sQuery(id+"F7.wireOp",EDGE,"E18");var subQ11=sQuery(id+"F7.wireOp",EDGE,"E23");var subQ12=sQuery(id+"F7.wireOp",EDGE,"E13.right");var subQ17=sQuery(id+"F7.wireOp",EDGE,"E16");var subQ18=sQuery(id+"F7.wireOp",EDGE,"E12.bottom");var subQ19=sQuery(id+"F7.wireOp",EDGE,"E21");Q1=makeQuery(id+"F16.boolean.opBoolean","SPLIT",FACE,{"disambiguationData":[TD([makeQuery(id+"F16.opExtrude","SWEPT_FACE",FACE,{"disambiguationData":[OSD([sQuery(id+"F15.wireOp",EDGE,"E28.MirrorCS")])]})])],"derivedFrom":makeQuery(id+"F13.boolean.opBoolean","SPLIT",FACE,{"disambiguationData":[TD([makeQuery(id+"F8.boolean.opBoolean","COPY",FACE,{"derivedFrom":makeQuery(id+"F8.opExtrude","SWEPT_FACE",FACE,{"disambiguationData":[OSD([subQ5])]})})])],"derivedFrom":makeQuery(id+"F8.boolean.opBoolean","COPY",FACE,{"derivedFrom":makeQuery(id+"F8.opExtrude","CAP_FACE",FACE,{"disambiguationData":[OSD([subQ5,subQ6,subQ4,subQ18,subQ1,sQuery(id+"F7.wireOp",EDGE,"E12.left"),subQ3,subQ12,subQ7,subQ9,subQ17,subQ0,subQ10,sQuery(id+"F7.wireOp",EDGE,"E19"),subQ8,subQ19,sQuery(id+"F7.wireOp",EDGE,"E22"),subQ11])],"isStart":false})})})});}
            var Q2;
            {var subQ0=sQuery(id+"F7.wireOp",EDGE,"E17");var subQ1=sQuery(id+"F7.wireOp",EDGE,"E12.top");var subQ3=sQuery(id+"F7.wireOp",EDGE,"E13.left");var subQ4=sQuery(id+"F7.wireOp",EDGE,"E11.right");var subQ5=sQuery(id+"F7.wireOp",EDGE,"E11.bottom");var subQ6=sQuery(id+"F7.wireOp",EDGE,"E11.left");var subQ7=sQuery(id+"F7.wireOp",EDGE,"E14.trimOffspring");var subQ8=sQuery(id+"F7.wireOp",EDGE,"E20");var subQ9=sQuery(id+"F7.wireOp",EDGE,"E15.trimOffspring");var subQ10=sQuery(id+"F7.wireOp",EDGE,"E18");var subQ11=sQuery(id+"F7.wireOp",EDGE,"E23");var subQ12=sQuery(id+"F7.wireOp",EDGE,"E13.right");var subQ17=sQuery(id+"F7.wireOp",EDGE,"E16");var subQ18=sQuery(id+"F7.wireOp",EDGE,"E12.bottom");var subQ19=sQuery(id+"F7.wireOp",EDGE,"E21");Q2=makeQuery(id+"F16.boolean.opBoolean","SPLIT",FACE,{"disambiguationData":[TD([makeQuery(id+"F16.opExtrude","SWEPT_FACE",FACE,{"disambiguationData":[OSD([sQuery(id+"F15.wireOp",EDGE,"E26")])]})])],"derivedFrom":makeQuery(id+"F13.boolean.opBoolean","SPLIT",FACE,{"disambiguationData":[TD([makeQuery(id+"F8.boolean.opBoolean","COPY",FACE,{"derivedFrom":makeQuery(id+"F8.opExtrude","SWEPT_FACE",FACE,{"disambiguationData":[OSD([subQ5])]})})])],"derivedFrom":makeQuery(id+"F8.boolean.opBoolean","COPY",FACE,{"derivedFrom":makeQuery(id+"F8.opExtrude","CAP_FACE",FACE,{"disambiguationData":[OSD([subQ5,subQ6,subQ4,subQ18,subQ1,sQuery(id+"F7.wireOp",EDGE,"E12.left"),subQ3,subQ12,subQ7,subQ9,subQ17,subQ0,subQ10,sQuery(id+"F7.wireOp",EDGE,"E19"),subQ8,subQ19,sQuery(id+"F7.wireOp",EDGE,"E22"),subQ11])],"isStart":false})})})});}
            extrude(context, id + "F17", {"entities" : qUnion([Q0, Q1, Q2]), "operationType" : NewBodyOperationType.ADD, "depth" : 1.27 * mm});
        }
        {
            var Q0;
            Q0=makeQuery(id+"F16.opExtrude","SWEPT_EDGE",EDGE,{"disambiguationData":[OSD([sQuery(id+"F15.wireOp",EDGE,"E34.bottom"),sQuery(id+"F15.wireOp",EDGE,"E34.left")])]});
            var Q1;
            Q1=makeQuery(id+"F17.opExtrude","SWEPT_EDGE",EDGE,{"disambiguationData":[OSD([sQuery(id+"F15.wireOp",EDGE,"E27.bottom"),sQuery(id+"F15.wireOp",EDGE,"E27.left")])]});
            var Q2;
            Q2=makeQuery(id+"F17.opExtrude","SWEPT_EDGE",EDGE,{"disambiguationData":[OSD([sQuery(id+"F15.wireOp",EDGE,"E27.bottom"),sQuery(id+"F15.wireOp",EDGE,"E27.right")])]});
            var Q3;
            Q3=makeQuery(id+"F17.opExtrude","SWEPT_EDGE",EDGE,{"disambiguationData":[OSD([sQuery(id+"F15.wireOp",EDGE,"E28.MirrorCS"),sQuery(id+"F15.wireOp",EDGE,"E29.MirrorCS")])]});
            var Q4;
            Q4=makeQuery(id+"F16.opExtrude","SWEPT_EDGE",EDGE,{"disambiguationData":[OSD([sQuery(id+"F15.wireOp",EDGE,"E34.bottom"),sQuery(id+"F15.wireOp",EDGE,"E34.right")])]});
            var Q5;
            Q5=makeQuery(id+"F17.opExtrude","SWEPT_EDGE",EDGE,{"disambiguationData":[OSD([sQuery(id+"F15.wireOp",EDGE,"E29.MirrorCS"),sQuery(id+"F15.wireOp",EDGE,"E31.MirrorCS")])]});
            var Q6;
            Q6=makeQuery(id+"F17.opExtrude","SWEPT_EDGE",EDGE,{"disambiguationData":[OSD([sQuery(id+"F15.wireOp",EDGE,"E30.MirrorCS"),sQuery(id+"F15.wireOp",EDGE,"E31.MirrorCS")])]});
            var Q7;
            Q7=makeQuery(id+"F17.opExtrude","SWEPT_EDGE",EDGE,{"disambiguationData":[OSD([sQuery(id+"F15.wireOp",EDGE,"E28.MirrorCS"),sQuery(id+"F15.wireOp",EDGE,"E30.MirrorCS")])]});
            var Q8;
            Q8=makeQuery(id+"F17.opExtrude","SWEPT_EDGE",EDGE,{"disambiguationData":[OSD([sQuery(id+"F15.wireOp",EDGE,"E27.top"),sQuery(id+"F15.wireOp",EDGE,"E27.left")])]});
            var Q9;
            Q9=makeQuery(id+"F17.opExtrude","SWEPT_EDGE",EDGE,{"disambiguationData":[OSD([sQuery(id+"F15.wireOp",EDGE,"E27.top"),sQuery(id+"F15.wireOp",EDGE,"E27.right")])]});
            var Q10;
            Q10=makeQuery(id+"F16.opExtrude","SWEPT_EDGE",EDGE,{"disambiguationData":[OSD([sQuery(id+"F15.wireOp",EDGE,"E34.top"),sQuery(id+"F15.wireOp",EDGE,"E34.left")])]});
            var Q11;
            Q11=makeQuery(id+"F16.opExtrude","SWEPT_EDGE",EDGE,{"disambiguationData":[OSD([sQuery(id+"F15.wireOp",EDGE,"E34.top"),sQuery(id+"F15.wireOp",EDGE,"E34.right")])]});
            var Q12;
            Q12=makeQuery(id+"F17.opExtrude","CAP_EDGE",EDGE,{"disambiguationData":[OSD([sQuery(id+"F15.wireOp",EDGE,"E26")])],"isStart":false});
            fillet(context, id + "F18", {"entities" : qUnion([Q0, Q1, Q2, Q3, Q4, Q5, Q6, Q7, Q8, Q9, Q10, Q11, Q12]), "radius" : 0.32 * mm, "tangentPropagation" : true, "allowEdgeOverflow" : false});
        }
        {
            var Q0;
            Q0=makeQuery(id+"F2.opExtrude","SWEPT_FACE",FACE,{"disambiguationData":[OSD([sQuery(id+"F0.wireOp",EDGE,"E3.top")])]});
            var sketch = newSketch(context, id + "F19", { "sketchPlane" : qUnion([Q0])});
            skCircle(sketch, "E36", {"center": v(-19.35, -3.47) * mm, "radius": 12.7 * mm});
            skSolve(sketch);
        }
        {
            var Q0;
            Q0 = qSketchRegion(id + "F19", true);
            extrude(context, id + "F20", {"entities" : qUnion([Q0]), "operationType" : NewBodyOperationType.REMOVE, "oppositeDirection" : true, "depth" : 12.7 * mm});
        }
        {
            var Q0;
            Q0=makeQuery(id+"F1.opExtrude","CAP_FACE",FACE,{"disambiguationData":[OSD([sQuery(id+"F0.wireOp",EDGE,"E0.top"),sQuery(id+"F0.wireOp",EDGE,"E0.left"),sQuery(id+"F0.wireOp",EDGE,"E0.right"),sQuery(id+"F0.wireOp",EDGE,"E1"),sQuery(id+"F0.wireOp",EDGE,"E3.bottom")])],"isStart":false});
            var sketch = newSketch(context, id + "F21", { "sketchPlane" : qUnion([Q0])});
            skLineSegment(sketch, "E37.top", {"start": v(-17.78, -18.35) * mm, "end": v(2.54, -18.35) * mm});
            skLineSegment(sketch, "E37.left", {"start": v(-17.78, -15.8) * mm, "end": v(-17.78, -18.35) * mm});
            skLineSegment(sketch, "E38", {"start": v(-17.78, -15.8) * mm, "end": v(2.54, -15.8) * mm});
            skLineSegment(sketch, "E39", {"start": v(2.54, -15.8) * mm, "end": v(2.54, -18.35) * mm});
            skLineSegment(sketch, "E40", {"start": v(2.54, -51.46) * mm, "end": v(2.54, 53.84) * mm});
            skPoint(sketch, "E40.startSnap0", {"position": v(2.54, -17.08) * mm});
            skLineSegment(sketch, "E41", {"start": v(2.54, 53.84) * mm, "end": v(5.08, 53.84) * mm});
            skLineSegment(sketch, "E42", {"start": v(5.08, 53.84) * mm, "end": v(5.08, -51.46) * mm});
            skLineSegment(sketch, "E43", {"start": v(5.08, -51.46) * mm, "end": v(2.54, -51.46) * mm});
            skSolve(sketch);
        }
        {
            var Q0;
            Q0 = qSketchRegion(id + "F21", true);
            extrude(context, id + "F22", {"entities" : qUnion([Q0]), "operationType" : NewBodyOperationType.REMOVE, "oppositeDirection" : true, "depth" : 1.27 * mm});
        }
        {
            var Q0;
            Q0=makeQuery(id+"F22.boolean.opBoolean","COPY",EDGE,{"derivedFrom":makeQuery(id+"F22.opExtrude","CAP_EDGE",EDGE,{"disambiguationData":[OSD([sQuery(id+"F21.wireOp",EDGE,"E38")])],"isStart":true})});
            var Q1;
            Q1=makeQuery(id+"F22.boolean.opBoolean","COPY",EDGE,{"derivedFrom":makeQuery(id+"F22.opExtrude","CAP_EDGE",EDGE,{"disambiguationData":[OSD([sQuery(id+"F21.wireOp",EDGE,"E37.top")])],"isStart":true})});
            var Q2;
            {var subQ0=sQuery(id+"F21.wireOp",EDGE,"E40");Q2=makeQuery(id+"F22.boolean.opBoolean","COPY",EDGE,{"derivedFrom":makeQuery(id+"F22.opExtrude","CAP_EDGE",EDGE,{"disambiguationData":[OSD([subQ0]),TDD([makeQuery(id+"F21.imprint","IMPRINT",EDGE,{"disambiguationData":[TD([[makeQuery(id+"F21.imprint","INTERSECT",VERTEX,{"derivedFrom":[subQ0,sQuery(id+"F21.wireOp",EDGE,"E43")]}),-1.0]])],"derivedFrom":subQ0}),makeQuery(id+"F21.imprint","IMPRINT",EDGE,{"disambiguationData":[TD([[makeQuery(id+"F21.imprint","INTERSECT",VERTEX,{"derivedFrom":[sQuery(id+"F21.wireOp",EDGE,"E37.top"),subQ0]}),1.0]])],"derivedFrom":subQ0})])],"isStart":true})});}
            var Q3;
            Q3=makeQuery(id+"F22.boolean.opBoolean","COPY",EDGE,{"derivedFrom":makeQuery(id+"F22.opExtrude","CAP_EDGE",EDGE,{"disambiguationData":[OSD([sQuery(id+"F21.wireOp",EDGE,"E42")])],"isStart":true})});
            var Q4;
            {var subQ0=sQuery(id+"F21.wireOp",EDGE,"E40");Q4=makeQuery(id+"F22.boolean.opBoolean","COPY",EDGE,{"derivedFrom":makeQuery(id+"F22.opExtrude","CAP_EDGE",EDGE,{"disambiguationData":[OSD([subQ0]),TDD([makeQuery(id+"F21.imprint","IMPRINT",EDGE,{"disambiguationData":[TD([[makeQuery(id+"F21.imprint","INTERSECT",VERTEX,{"derivedFrom":[sQuery(id+"F21.wireOp",EDGE,"E38"),subQ0]}),-1.0]])],"derivedFrom":subQ0}),makeQuery(id+"F21.imprint","IMPRINT",EDGE,{"disambiguationData":[TD([[makeQuery(id+"F21.imprint","INTERSECT",VERTEX,{"derivedFrom":[subQ0,sQuery(id+"F21.wireOp",EDGE,"E41")]}),1.0]])],"derivedFrom":subQ0})])],"isStart":true})});}
            fillet(context, id + "F23", {"entities" : qUnion([Q0, Q1, Q2, Q3, Q4]), "radius" : 0.32 * mm, "tangentPropagation" : true, "allowEdgeOverflow" : false});
        }
        {
            var Q0;
            Q0=makeQuery(id+"F1.opExtrude","CAP_FACE",FACE,{"disambiguationData":[OSD([sQuery(id+"F0.wireOp",EDGE,"E0.top"),sQuery(id+"F0.wireOp",EDGE,"E0.left"),sQuery(id+"F0.wireOp",EDGE,"E0.right"),sQuery(id+"F0.wireOp",EDGE,"E1"),sQuery(id+"F0.wireOp",EDGE,"E3.bottom")])],"isStart":true});
            var sketch = newSketch(context, id + "F24", { "sketchPlane" : qUnion([Q0])});
            skLineSegment(sketch, "E44", {"start": v(17.78, -15.8) * mm, "end": v(-2.54, -15.8) * mm});
            skLineSegment(sketch, "E45", {"start": v(-2.54, -15.8) * mm, "end": v(-2.54, -18.35) * mm});
            skLineSegment(sketch, "E46", {"start": v(-2.54, -18.35) * mm, "end": v(17.78, -18.35) * mm});
            skLineSegment(sketch, "E47", {"start": v(17.78, -18.35) * mm, "end": v(17.78, -15.8) * mm});
            skLineSegment(sketch, "E48", {"start": v(-2.54, -53.17) * mm, "end": v(-5.08, -53.17) * mm});
            skLineSegment(sketch, "E49", {"start": v(-5.08, -53.17) * mm, "end": v(-5.08, 58.98) * mm});
            skLineSegment(sketch, "E50", {"start": v(-5.08, 58.98) * mm, "end": v(-2.54, 58.98) * mm});
            skLineSegment(sketch, "E51", {"start": v(-2.54, 58.98) * mm, "end": v(-2.54, -53.17) * mm});
            skSolve(sketch);
        }
        {
            var Q0;
            Q0 = qSketchRegion(id + "F24", true);
            extrude(context, id + "F25", {"entities" : qUnion([Q0]), "operationType" : NewBodyOperationType.REMOVE, "oppositeDirection" : true, "depth" : 0.64 * mm});
        }
        {
            var Q0;
            Q0=makeQuery(id+"F25.boolean.opBoolean","COPY",EDGE,{"derivedFrom":makeQuery(id+"F25.opExtrude","CAP_EDGE",EDGE,{"disambiguationData":[OSD([sQuery(id+"F24.wireOp",EDGE,"E49")])],"isStart":true})});
            var Q1;
            {var subQ0=sQuery(id+"F24.wireOp",EDGE,"E51");Q1=makeQuery(id+"F25.boolean.opBoolean","COPY",EDGE,{"derivedFrom":makeQuery(id+"F25.opExtrude","CAP_EDGE",EDGE,{"disambiguationData":[OSD([subQ0]),TDD([makeQuery(id+"F24.imprint","IMPRINT",EDGE,{"disambiguationData":[TD([[makeQuery(id+"F24.imprint","INTERSECT",VERTEX,{"derivedFrom":[sQuery(id+"F24.wireOp",EDGE,"E46"),subQ0]}),-1.0]])],"derivedFrom":subQ0}),makeQuery(id+"F24.imprint","IMPRINT",EDGE,{"disambiguationData":[TD([[makeQuery(id+"F24.imprint","INTERSECT",VERTEX,{"derivedFrom":[sQuery(id+"F24.wireOp",EDGE,"E48"),subQ0]}),1.0]])],"derivedFrom":subQ0})])],"isStart":true})});}
            var Q2;
            Q2=makeQuery(id+"F25.boolean.opBoolean","COPY",EDGE,{"derivedFrom":makeQuery(id+"F25.opExtrude","CAP_EDGE",EDGE,{"disambiguationData":[OSD([sQuery(id+"F24.wireOp",EDGE,"E46")])],"isStart":true})});
            var Q3;
            Q3=makeQuery(id+"F25.boolean.opBoolean","COPY",EDGE,{"derivedFrom":makeQuery(id+"F25.opExtrude","CAP_EDGE",EDGE,{"disambiguationData":[OSD([sQuery(id+"F24.wireOp",EDGE,"E44")])],"isStart":true})});
            var Q4;
            {var subQ0=sQuery(id+"F24.wireOp",EDGE,"E51");Q4=makeQuery(id+"F25.boolean.opBoolean","COPY",EDGE,{"derivedFrom":makeQuery(id+"F25.opExtrude","CAP_EDGE",EDGE,{"disambiguationData":[OSD([subQ0]),TDD([makeQuery(id+"F24.imprint","IMPRINT",EDGE,{"disambiguationData":[TD([[makeQuery(id+"F24.imprint","INTERSECT",VERTEX,{"derivedFrom":[sQuery(id+"F24.wireOp",EDGE,"E50"),subQ0]}),-1.0]])],"derivedFrom":subQ0}),makeQuery(id+"F24.imprint","IMPRINT",EDGE,{"disambiguationData":[TD([[makeQuery(id+"F24.imprint","INTERSECT",VERTEX,{"derivedFrom":[sQuery(id+"F24.wireOp",EDGE,"E44"),subQ0]}),1.0]])],"derivedFrom":subQ0})])],"isStart":true})});}
            fillet(context, id + "F26", {"entities" : qUnion([Q0, Q1, Q2, Q3, Q4]), "radius" : 0.32 * mm, "tangentPropagation" : true, "allowEdgeOverflow" : false});
        }
        {
            var Q0;
            Q0=makeQuery(id+"F22.boolean.opBoolean","COPY",EDGE,{"derivedFrom":makeQuery(id+"F22.opExtrude","CAP_EDGE",EDGE,{"disambiguationData":[OSD([sQuery(id+"F21.wireOp",EDGE,"E37.left")])],"isStart":false})});
            var Q1;
            Q1=makeQuery(id+"F25.boolean.opBoolean","COPY",EDGE,{"derivedFrom":makeQuery(id+"F25.opExtrude","CAP_EDGE",EDGE,{"disambiguationData":[OSD([sQuery(id+"F24.wireOp",EDGE,"E47")])],"isStart":false})});
            fillet(context, id + "F27", {"entities" : qUnion([Q0, Q1]), "radius" : 0.32 * mm, "tangentPropagation" : true, "allowEdgeOverflow" : false});
        }
        {
            var Q0;
            Q0=makeQuery(id+"F1.opExtrude","SWEPT_FACE",FACE,{"disambiguationData":[OSD([sQuery(id+"F0.wireOp",EDGE,"E0.top")])]});
            var sketch = newSketch(context, id + "F28", { "sketchPlane" : qUnion([Q0])});
            skLineSegment(sketch, "E52.bottom", {"start": v(-44.9, 5.08) * mm, "end": v(-35.1, 5.08) * mm});
            skLineSegment(sketch, "E52.top", {"start": v(-44.9, 2.54) * mm, "end": v(-35.1, 2.54) * mm});
            skLineSegment(sketch, "E52.left", {"start": v(-44.9, 5.08) * mm, "end": v(-44.9, 2.54) * mm});
            skLineSegment(sketch, "E52.right", {"start": v(46.78, 5.08) * mm, "end": v(46.78, 2.54) * mm});
            skLineSegment(sketch, "E53", {"start": v(-35.1, 5.08) * mm, "end": v(-35.1, 2.54) * mm});
            skLineSegment(sketch, "E54", {"start": v(34.88, 2.54) * mm, "end": v(34.88, 5.08) * mm});
            skLineSegment(sketch, "E55.trimOffspring", {"start": v(34.88, 5.08) * mm, "end": v(46.78, 5.08) * mm});
            skLineSegment(sketch, "E56.trimOffspring", {"start": v(34.88, 2.54) * mm, "end": v(46.78, 2.54) * mm});
            skSolve(sketch);
        }
        {
            var Q0;
            {var subQ0=sQuery(id+"F28.wireOp",EDGE,"E52.bottom");var subQ1=sQuery(id+"F0.wireOp",EDGE,"E0.top");var subQ2=makeQuery(id+"F1.opExtrude","SWEPT_FACE",FACE,{"disambiguationData":[OSD([subQ1])]});var subQ3=subQ2;var subQ4=makeQuery(id+"F3.opFillet","BLEND_EDGE",EDGE,{"blendedFrom":[makeQuery(id+"F1.opExtrude","CAP_EDGE",EDGE,{"disambiguationData":[OSD([subQ1])],"isStart":true}),subQ3],"blendedInto":[subQ3]});var subQ5=makeQuery(id+"F28.imprint","INTERSECT",VERTEX,{"derivedFrom":[subQ4,subQ0]});Q0=makeQuery(id+"F28.imprint","IMPRINT",FACE,{"disambiguationData":[TD([[makeQuery(id+"F28.imprint","IMPRINT",EDGE,{"disambiguationData":[TD([[subQ5,-1.0]])],"derivedFrom":subQ4}),1.0]])]});}
            var Q1;
            {var subQ0=sQuery(id+"F28.wireOp",EDGE,"E52.left");Q1=makeQuery(id+"F28.imprint","IMPRINT",FACE,{"disambiguationData":[TD([[makeQuery(id+"F28.imprint","IMPRINT",EDGE,{"derivedFrom":subQ0}),1.0]])]});}
            var Q2;
            {var subQ0=sQuery(id+"F28.wireOp",EDGE,"E52.right");Q2=makeQuery(id+"F28.imprint","IMPRINT",FACE,{"disambiguationData":[TD([[makeQuery(id+"F28.imprint","IMPRINT",EDGE,{"derivedFrom":subQ0}),-1.0]])]});}
            extrude(context, id + "F29", {"entities" : qUnion([Q0, Q1, Q2]), "operationType" : NewBodyOperationType.REMOVE, "oppositeDirection" : true, "depth" : 0.64 * mm});
        }
        {
            var Q0;
            Q0=makeQuery(id+"F29.boolean.opBoolean","COPY",EDGE,{"derivedFrom":makeQuery(id+"F29.opExtrude","CAP_EDGE",EDGE,{"disambiguationData":[OSD([sQuery(id+"F28.wireOp",EDGE,"E52.bottom")])],"isStart":true})});
            var Q1;
            Q1=makeQuery(id+"F29.boolean.opBoolean","COPY",EDGE,{"derivedFrom":makeQuery(id+"F29.opExtrude","CAP_EDGE",EDGE,{"disambiguationData":[OSD([sQuery(id+"F28.wireOp",EDGE,"E52.top")])],"isStart":true})});
            var Q2;
            Q2=makeQuery(id+"F29.boolean.opBoolean","INTERSECT",EDGE,{"derivedFrom":[makeQuery(id+"F22.boolean.opBoolean","COPY",FACE,{"derivedFrom":makeQuery(id+"F22.opExtrude","CAP_FACE",FACE,{"disambiguationData":[OSD([sQuery(id+"F21.wireOp",EDGE,"E37.top"),sQuery(id+"F21.wireOp",EDGE,"E37.left"),sQuery(id+"F21.wireOp",EDGE,"E38"),sQuery(id+"F21.wireOp",EDGE,"E40"),sQuery(id+"F21.wireOp",EDGE,"E41"),sQuery(id+"F21.wireOp",EDGE,"E42"),sQuery(id+"F21.wireOp",EDGE,"E43")])],"isStart":false})}),makeQuery(id+"F29.opExtrude","CAP_FACE",FACE,{"disambiguationData":[OSD([sQuery(id+"F28.wireOp",EDGE,"E52.bottom"),sQuery(id+"F28.wireOp",EDGE,"E52.top"),sQuery(id+"F28.wireOp",EDGE,"E52.left"),sQuery(id+"F28.wireOp",EDGE,"E52.right")])],"isStart":false})]});
            var Q3;
            Q3=makeQuery(id+"F29.boolean.opBoolean","INTERSECT",EDGE,{"derivedFrom":[makeQuery(id+"F25.boolean.opBoolean","COPY",FACE,{"derivedFrom":makeQuery(id+"F25.opExtrude","CAP_FACE",FACE,{"disambiguationData":[OSD([sQuery(id+"F24.wireOp",EDGE,"E44"),sQuery(id+"F24.wireOp",EDGE,"E46"),sQuery(id+"F24.wireOp",EDGE,"E47"),sQuery(id+"F24.wireOp",EDGE,"E48"),sQuery(id+"F24.wireOp",EDGE,"E49"),sQuery(id+"F24.wireOp",EDGE,"E50"),sQuery(id+"F24.wireOp",EDGE,"E51")])],"isStart":false})}),makeQuery(id+"F29.opExtrude","CAP_FACE",FACE,{"disambiguationData":[OSD([sQuery(id+"F28.wireOp",EDGE,"E52.bottom"),sQuery(id+"F28.wireOp",EDGE,"E52.top"),sQuery(id+"F28.wireOp",EDGE,"E52.left"),sQuery(id+"F28.wireOp",EDGE,"E52.right")])],"isStart":false})]});
            var Q4;
            {var subQ0=sQuery(id+"F0.wireOp",EDGE,"E0.top");Q4=makeQuery(id+"F29.boolean.opBoolean","INTERSECT",EDGE,{"derivedFrom":[makeQuery(id+"F3.opFillet","BLEND_FACE",FACE,{"disambiguationData":[OSD([subQ0]),TDD([makeQuery(id+"F1.opExtrude","CAP_EDGE",EDGE,{"disambiguationData":[OSD([subQ0])],"isStart":true})])]}),makeQuery(id+"F29.opExtrude","SWEPT_FACE",FACE,{"disambiguationData":[OSD([sQuery(id+"F28.wireOp",EDGE,"E52.bottom")])]})]});}
            var Q5;
            {var subQ0=sQuery(id+"F0.wireOp",EDGE,"E0.top");Q5=makeQuery(id+"F29.boolean.opBoolean","INTERSECT",EDGE,{"derivedFrom":[makeQuery(id+"F3.opFillet","BLEND_FACE",FACE,{"disambiguationData":[OSD([subQ0]),TDD([makeQuery(id+"F1.opExtrude","CAP_EDGE",EDGE,{"disambiguationData":[OSD([subQ0])],"isStart":true})])]}),makeQuery(id+"F29.opExtrude","SWEPT_FACE",FACE,{"disambiguationData":[OSD([sQuery(id+"F28.wireOp",EDGE,"E52.top")])]})]});}
            fillet(context, id + "F30", {"entities" : qUnion([Q0, Q1, Q2, Q3, Q4, Q5]), "radius" : 0.32 * mm, "tangentPropagation" : true, "allowEdgeOverflow" : false});
        }
        {
            var Q0;
            {var subQ13=sQuery(id+"F0.wireOp",EDGE,"E0.right");var subQ16=sQuery(id+"F4.wireOp",EDGE,"E5.bottom");Q0=makeQuery(id+"F8.boolean.opBoolean","SPLIT",FACE,{"disambiguationData":[TD([makeQuery(id+"F5.opExtrude","SWEPT_FACE",FACE,{"disambiguationData":[OSD([subQ16])]})])],"derivedFrom":makeQuery(id+"F1.opExtrude","SWEPT_FACE",FACE,{"disambiguationData":[OSD([subQ13])]})});}
            var sketch = newSketch(context, id + "F31", { "sketchPlane" : qUnion([Q0])});
            skLineSegment(sketch, "E57", {"start": v(-36.83, 49.53) * mm, "end": v(-26.9, 57.44) * mm});
            skLineSegment(sketch, "E58", {"start": v(36.83, 49.53) * mm, "end": v(26.9, 57.44) * mm});
            skLineSegment(sketch, "E59", {"start": v(-26.9, 57.44) * mm, "end": v(26.9, 57.44) * mm});
            skLineSegment(sketch, "E60", {"start": v(-35.23, 50.8) * mm, "end": v(35.23, 50.8) * mm});
            skLineSegment(sketch, "E61", {"start": v(-16.19, 43.98) * mm, "end": v(-37.6, 70.9) * mm, "construction": true});
            skLineSegment(sketch, "E62", {"start": v(18.84, 47.31) * mm, "end": v(34.94, 67.56) * mm, "construction": true});
            skSolve(sketch);
        }
        {
            var Q0;
            {var subQ0=sQuery(id+"F31.wireOp",EDGE,"E59");Q0=makeQuery(id+"F31.imprint","IMPRINT",FACE,{"disambiguationData":[TD([[makeQuery(id+"F31.imprint","IMPRINT",EDGE,{"derivedFrom":subQ0}),-1.0]])]});}
            extrude(context, id + "F32", {"entities" : qUnion([Q0]), "operationType" : NewBodyOperationType.ADD, "oppositeDirection" : true, "depth" : 38.1 * mm});
        }
        {
            var Q0;
            Q0=qCreatedBy(makeId("Right.planeOp"),FACE);
            var sketch = newSketch(context, id + "F33", { "sketchPlane" : qUnion([Q0])});
            skLineSegment(sketch, "E63", {"start": v(-25.34, 45.06) * mm, "end": v(-2.89, 61.9) * mm});
            skLineSegment(sketch, "E64", {"start": v(-2.89, 61.9) * mm, "end": v(-30.27, 56.86) * mm});
            skLineSegment(sketch, "E65", {"start": v(-30.27, 56.86) * mm, "end": v(-25.34, 45.06) * mm});
            skSolve(sketch);
        }
        {
            var Q0;
            Q0 = qSketchRegion(id + "F33", true);
            extrude(context, id + "F34", {"entities" : qUnion([Q0]), "operationType" : NewBodyOperationType.REMOVE, "endBound" : BoundingType.SYMMETRIC, "oppositeDirection" : true, "depth" : 76.2 * mm});
        }
        {
            var Q0;
            Q0=makeQuery(id+"F34.boolean.opBoolean","INTERSECT",EDGE,{"derivedFrom":[makeQuery(id+"F32.opExtrude","SWEPT_FACE",FACE,{"disambiguationData":[OSD([sQuery(id+"F31.wireOp",EDGE,"E57")])]}),makeQuery(id+"F34.opExtrude","SWEPT_FACE",FACE,{"disambiguationData":[OSD([sQuery(id+"F33.wireOp",EDGE,"E63")])]})]});
            var Q1;
            Q1=makeQuery(id+"F34.boolean.opBoolean","INTERSECT",EDGE,{"derivedFrom":[makeQuery(id+"F32.opExtrude","SWEPT_FACE",FACE,{"disambiguationData":[OSD([sQuery(id+"F31.wireOp",EDGE,"E59")])]}),makeQuery(id+"F34.opExtrude","SWEPT_FACE",FACE,{"disambiguationData":[OSD([sQuery(id+"F33.wireOp",EDGE,"E63")])]})]});
            var Q2;
            Q2=makeQuery(id+"F32.opExtrude","SWEPT_EDGE",EDGE,{"disambiguationData":[OSD([sQuery(id+"F31.wireOp",EDGE,"E57"),sQuery(id+"F31.wireOp",EDGE,"E59")])]});
            var Q3;
            Q3=makeQuery(id+"F34.boolean.opBoolean","INTERSECT",EDGE,{"derivedFrom":[makeQuery(id+"F32.opExtrude","SWEPT_FACE",FACE,{"disambiguationData":[OSD([sQuery(id+"F31.wireOp",EDGE,"E58")])]}),makeQuery(id+"F34.opExtrude","SWEPT_FACE",FACE,{"disambiguationData":[OSD([sQuery(id+"F33.wireOp",EDGE,"E63")])]})]});
            var Q4;
            Q4=makeQuery(id+"F32.opExtrude","SWEPT_EDGE",EDGE,{"disambiguationData":[OSD([sQuery(id+"F31.wireOp",EDGE,"E58"),sQuery(id+"F31.wireOp",EDGE,"E59")])]});
            fillet(context, id + "F35", {"entities" : qUnion([Q0, Q1, Q2, Q3, Q4]), "radius" : 1.27 * mm, "tangentPropagation" : true, "allowEdgeOverflow" : false});
        }
        {
            var Q0;
            {var subQ13=sQuery(id+"F0.wireOp",EDGE,"E0.right");var subQ16=sQuery(id+"F4.wireOp",EDGE,"E5.bottom");Q0=makeQuery(id+"F8.boolean.opBoolean","SPLIT",FACE,{"disambiguationData":[TD([makeQuery(id+"F5.opExtrude","SWEPT_FACE",FACE,{"disambiguationData":[OSD([subQ16])]})])],"derivedFrom":makeQuery(id+"F1.opExtrude","SWEPT_FACE",FACE,{"disambiguationData":[OSD([subQ13])]})});}
            var sketch = newSketch(context, id + "F36", { "sketchPlane" : qUnion([Q0])});
            skLineSegment(sketch, "E66", {"start": v(-25.4, 56.14) * mm, "end": v(-20.54, 52.05) * mm});
            skLineSegment(sketch, "E67", {"start": v(-20.54, 52.05) * mm, "end": v(20.54, 52.05) * mm});
            skLineSegment(sketch, "E68", {"start": v(20.54, 52.05) * mm, "end": v(25.4, 56.14) * mm});
            skLineSegment(sketch, "E69", {"start": v(25.4, 56.14) * mm, "end": v(-25.4, 56.14) * mm});
            skSolve(sketch);
        }
        {
            var Q0;
            Q0 = qSketchRegion(id + "F36", true);
            extrude(context, id + "F37", {"entities" : qUnion([Q0]), "operationType" : NewBodyOperationType.REMOVE, "oppositeDirection" : true, "depth" : 12.7 * mm});
        }
        {
            var Q0;
            Q0=makeQuery(id+"F37.boolean.opBoolean","INTERSECT",EDGE,{"derivedFrom":[makeQuery(id+"F34.boolean.opBoolean","COPY",FACE,{"derivedFrom":makeQuery(id+"F34.opExtrude","SWEPT_FACE",FACE,{"disambiguationData":[OSD([sQuery(id+"F33.wireOp",EDGE,"E63")])]})}),makeQuery(id+"F37.opExtrude","SWEPT_FACE",FACE,{"disambiguationData":[OSD([sQuery(id+"F36.wireOp",EDGE,"E68")])]})]});
            var Q1;
            Q1=makeQuery(id+"F37.boolean.opBoolean","INTERSECT",EDGE,{"derivedFrom":[makeQuery(id+"F34.boolean.opBoolean","COPY",FACE,{"derivedFrom":makeQuery(id+"F34.opExtrude","SWEPT_FACE",FACE,{"disambiguationData":[OSD([sQuery(id+"F33.wireOp",EDGE,"E63")])]})}),makeQuery(id+"F37.opExtrude","SWEPT_FACE",FACE,{"disambiguationData":[OSD([sQuery(id+"F36.wireOp",EDGE,"E69")])]})]});
            var Q2;
            Q2=makeQuery(id+"F37.boolean.opBoolean","INTERSECT",EDGE,{"derivedFrom":[makeQuery(id+"F34.boolean.opBoolean","COPY",FACE,{"derivedFrom":makeQuery(id+"F34.opExtrude","SWEPT_FACE",FACE,{"disambiguationData":[OSD([sQuery(id+"F33.wireOp",EDGE,"E63")])]})}),makeQuery(id+"F37.opExtrude","SWEPT_FACE",FACE,{"disambiguationData":[OSD([sQuery(id+"F36.wireOp",EDGE,"E66")])]})]});
            var Q3;
            Q3=makeQuery(id+"F37.boolean.opBoolean","INTERSECT",EDGE,{"derivedFrom":[makeQuery(id+"F34.boolean.opBoolean","COPY",FACE,{"derivedFrom":makeQuery(id+"F34.opExtrude","SWEPT_FACE",FACE,{"disambiguationData":[OSD([sQuery(id+"F33.wireOp",EDGE,"E63")])]})}),makeQuery(id+"F37.opExtrude","SWEPT_FACE",FACE,{"disambiguationData":[OSD([sQuery(id+"F36.wireOp",EDGE,"E67")])]})]});
            var Q4;
            Q4=makeQuery(id+"F37.boolean.opBoolean","COPY",EDGE,{"derivedFrom":makeQuery(id+"F37.opExtrude","SWEPT_EDGE",EDGE,{"disambiguationData":[OSD([sQuery(id+"F36.wireOp",EDGE,"E66"),sQuery(id+"F36.wireOp",EDGE,"E67")])]})});
            var Q5;
            Q5=makeQuery(id+"F37.boolean.opBoolean","COPY",EDGE,{"derivedFrom":makeQuery(id+"F37.opExtrude","SWEPT_EDGE",EDGE,{"disambiguationData":[OSD([sQuery(id+"F36.wireOp",EDGE,"E67"),sQuery(id+"F36.wireOp",EDGE,"E68")])]})});
            fillet(context, id + "F38", {"entities" : qUnion([Q0, Q1, Q2, Q3, Q4, Q5]), "radius" : 0.64 * mm, "tangentPropagation" : true, "allowEdgeOverflow" : false});
        }
        {
            var Q0;
            Q0=makeQuery(id+"F32.opExtrude","SWEPT_FACE",FACE,{"disambiguationData":[OSD([sQuery(id+"F31.wireOp",EDGE,"E59")])]});
            var sketch = newSketch(context, id + "F39", { "sketchPlane" : qUnion([Q0])});
            skLineSegment(sketch, "E70.bottom", {"start": v(-52.6, 5.08) * mm, "end": v(48.52, 5.08) * mm});
            skLineSegment(sketch, "E70.top", {"start": v(-52.6, 2.54) * mm, "end": v(48.52, 2.54) * mm});
            skLineSegment(sketch, "E70.left", {"start": v(-52.6, 5.08) * mm, "end": v(-52.6, 2.54) * mm});
            skLineSegment(sketch, "E70.right", {"start": v(48.52, 5.08) * mm, "end": v(48.52, 2.54) * mm});
            skSolve(sketch);
        }
        {
            var Q0;
            Q0 = qSketchRegion(id + "F39", true);
            extrude(context, id + "F40", {"entities" : qUnion([Q0]), "operationType" : NewBodyOperationType.REMOVE, "oppositeDirection" : true, "depth" : 0.64 * mm});
        }
        {
            var Q0;
            Q0=sQuery(id+"F31.wireOp",EDGE,"E61");
            cPlane(context, id + "F41", {"entities" : qUnion([Q0]), "cplaneType" : CPlaneType.MID_PLANE, "offset" : 25.4 * mm, "width" : 152.4 * mm, "height" : 152.4 * mm});
        }
        {
            var Q0;
            Q0=sQuery(id+"F31.wireOp",EDGE,"E62");
            cPlane(context, id + "F42", {"entities" : qUnion([Q0]), "cplaneType" : CPlaneType.MID_PLANE, "offset" : 25.4 * mm, "width" : 152.4 * mm, "height" : 152.4 * mm});
        }
        {
            var Q0;
            Q0=qCreatedBy(id+"F41.planeOp",FACE);
            var sketch = newSketch(context, id + "F43", { "sketchPlane" : qUnion([Q0])});
            skLineSegment(sketch, "E71", {"start": v(14.45, 5.14) * mm, "end": v(4.05, 5.14) * mm});
            skLineSegment(sketch, "E72", {"start": v(4.05, 5.14) * mm, "end": v(4.05, 2.6) * mm});
            skLineSegment(sketch, "E73", {"start": v(4.05, 2.6) * mm, "end": v(14.45, 2.6) * mm});
            skLineSegment(sketch, "E74", {"start": v(14.45, 2.6) * mm, "end": v(14.45, 5.14) * mm});
            skSolve(sketch);
        }
        {
            var Q0;
            Q0 = qSketchRegion(id + "F43", true);
            extrude(context, id + "F44", {"entities" : qUnion([Q0]), "operationType" : NewBodyOperationType.REMOVE, "oppositeDirection" : true, "depth" : 0.64 * mm});
        }
        {
            var Q0;
            Q0=makeQuery(id+"F44.boolean.opBoolean","COPY",EDGE,{"derivedFrom":makeQuery(id+"F44.opExtrude","CAP_EDGE",EDGE,{"disambiguationData":[OSD([sQuery(id+"F43.wireOp",EDGE,"E71")])],"isStart":true})});
            var Q1;
            Q1=makeQuery(id+"F44.boolean.opBoolean","COPY",EDGE,{"derivedFrom":makeQuery(id+"F44.opExtrude","CAP_EDGE",EDGE,{"disambiguationData":[OSD([sQuery(id+"F43.wireOp",EDGE,"E73")])],"isStart":true})});
            fillet(context, id + "F45", {"entities" : qUnion([Q0, Q1]), "radius" : 0.32 * mm, "tangentPropagation" : true, "allowEdgeOverflow" : false});
        }
        {
            var Q0;
            Q0=makeQuery(id+"F40.boolean.opBoolean","COPY",EDGE,{"derivedFrom":makeQuery(id+"F40.opExtrude","CAP_EDGE",EDGE,{"disambiguationData":[OSD([sQuery(id+"F39.wireOp",EDGE,"E70.bottom")])],"isStart":true})});
            var Q1;
            Q1=makeQuery(id+"F40.boolean.opBoolean","COPY",EDGE,{"derivedFrom":makeQuery(id+"F40.opExtrude","CAP_EDGE",EDGE,{"disambiguationData":[OSD([sQuery(id+"F39.wireOp",EDGE,"E70.top")])],"isStart":true})});
            fillet(context, id + "F46", {"entities" : qUnion([Q0, Q1]), "radius" : 0.32 * mm, "tangentPropagation" : true, "allowEdgeOverflow" : false});
        }
        {
            var Q0;
            Q0=qCreatedBy(id+"F42.planeOp",FACE);
            var sketch = newSketch(context, id + "F47", { "sketchPlane" : qUnion([Q0])});
            skLineSegment(sketch, "E75.bottom", {"start": v(-14.33, 2.54) * mm, "end": v(-4.05, 2.54) * mm});
            skLineSegment(sketch, "E75.top", {"start": v(-14.33, 5.08) * mm, "end": v(-4.05, 5.08) * mm});
            skLineSegment(sketch, "E75.left", {"start": v(-14.33, 2.54) * mm, "end": v(-14.33, 5.08) * mm});
            skLineSegment(sketch, "E75.right", {"start": v(-4.05, 2.54) * mm, "end": v(-4.05, 5.08) * mm});
            skSolve(sketch);
        }
        {
            var Q0;
            Q0=makeQuery(id+"F47.imprint","IMPRINT",FACE,{"disambiguationData":[TD([[makeQuery(id+"F47.imprint","IMPRINT",EDGE,{"derivedFrom":sQuery(id+"F47.wireOp",EDGE,"E75.bottom")}),1.0]])]});
            extrude(context, id + "F48", {"entities" : qUnion([Q0]), "operationType" : NewBodyOperationType.REMOVE, "oppositeDirection" : true, "depth" : 0.64 * mm});
        }
        {
            var Q0;
            {var subQ0=sQuery(id+"F28.wireOp",EDGE,"E54");Q0=makeQuery(id+"F28.imprint","IMPRINT",FACE,{"disambiguationData":[TD([[makeQuery(id+"F28.imprint","IMPRINT",EDGE,{"derivedFrom":subQ0}),-1.0]])]});}
            extrude(context, id + "F49", {"entities" : qUnion([Q0]), "operationType" : NewBodyOperationType.REMOVE, "oppositeDirection" : true, "depth" : 0.64 * mm});
        }
        {
            var Q0;
            Q0=makeQuery(id+"F48.boolean.opBoolean","INTERSECT",EDGE,{"derivedFrom":[makeQuery(id+"F40.boolean.opBoolean","COPY",FACE,{"derivedFrom":makeQuery(id+"F40.opExtrude","CAP_FACE",FACE,{"disambiguationData":[OSD([sQuery(id+"F39.wireOp",EDGE,"E70.bottom"),sQuery(id+"F39.wireOp",EDGE,"E70.top"),sQuery(id+"F39.wireOp",EDGE,"E70.left"),sQuery(id+"F39.wireOp",EDGE,"E70.right")])],"isStart":false})}),makeQuery(id+"F48.opExtrude","SWEPT_FACE",FACE,{"disambiguationData":[OSD([sQuery(id+"F47.wireOp",EDGE,"E75.left")])]})]});
            var Q1;
            Q1=makeQuery(id+"F48.boolean.opBoolean","COPY",EDGE,{"derivedFrom":makeQuery(id+"F48.opExtrude","CAP_EDGE",EDGE,{"disambiguationData":[OSD([sQuery(id+"F47.wireOp",EDGE,"E75.top")])],"isStart":true})});
            var Q2;
            Q2=makeQuery(id+"F48.boolean.opBoolean","COPY",EDGE,{"derivedFrom":makeQuery(id+"F48.opExtrude","CAP_EDGE",EDGE,{"disambiguationData":[OSD([sQuery(id+"F47.wireOp",EDGE,"E75.bottom")])],"isStart":true})});
            fillet(context, id + "F50", {"entities" : qUnion([Q0, Q1, Q2]), "radius" : 0.32 * mm, "tangentPropagation" : true, "allowEdgeOverflow" : false});
        }
        {
            var Q0;
            Q0=makeQuery(id+"F49.boolean.opBoolean","COPY",EDGE,{"derivedFrom":makeQuery(id+"F49.opExtrude","CAP_EDGE",EDGE,{"disambiguationData":[OSD([sQuery(id+"F28.wireOp",EDGE,"E55.trimOffspring")])],"isStart":true})});
            var Q1;
            Q1=makeQuery(id+"F49.boolean.opBoolean","COPY",EDGE,{"derivedFrom":makeQuery(id+"F49.opExtrude","CAP_EDGE",EDGE,{"disambiguationData":[OSD([sQuery(id+"F28.wireOp",EDGE,"E56.trimOffspring")])],"isStart":true})});
            var Q2;
            Q2=makeQuery(id+"F49.boolean.opBoolean","COPY",EDGE,{"derivedFrom":makeQuery(id+"F49.opExtrude","CAP_EDGE",EDGE,{"disambiguationData":[OSD([sQuery(id+"F0.wireOp",EDGE,"E0.top")])],"isStart":false})});
            fillet(context, id + "F51", {"entities" : qUnion([Q0, Q1, Q2]), "radius" : 0.32 * mm, "tangentPropagation" : true, "allowEdgeOverflow" : false});
        }
        {
            var Q0;
            Q0=makeQuery(id+"F44.boolean.opBoolean","INTERSECT",EDGE,{"derivedFrom":[makeQuery(id+"F40.boolean.opBoolean","COPY",FACE,{"derivedFrom":makeQuery(id+"F40.opExtrude","CAP_FACE",FACE,{"disambiguationData":[OSD([sQuery(id+"F39.wireOp",EDGE,"E70.bottom"),sQuery(id+"F39.wireOp",EDGE,"E70.top"),sQuery(id+"F39.wireOp",EDGE,"E70.left"),sQuery(id+"F39.wireOp",EDGE,"E70.right")])],"isStart":false})}),makeQuery(id+"F44.opExtrude","SWEPT_FACE",FACE,{"disambiguationData":[OSD([sQuery(id+"F43.wireOp",EDGE,"E74")])]})]});
            fillet(context, id + "F52", {"entities" : qUnion([Q0]), "radius" : 0.32 * mm, "tangentPropagation" : true, "allowEdgeOverflow" : false});
        }
        {
            var Q0;
            {var subQ0=sQuery(id+"F7.wireOp",EDGE,"E17");var subQ1=sQuery(id+"F7.wireOp",EDGE,"E12.top");var subQ3=sQuery(id+"F7.wireOp",EDGE,"E13.left");var subQ4=sQuery(id+"F7.wireOp",EDGE,"E11.right");var subQ5=sQuery(id+"F7.wireOp",EDGE,"E11.bottom");var subQ6=sQuery(id+"F7.wireOp",EDGE,"E11.left");var subQ7=sQuery(id+"F7.wireOp",EDGE,"E14.trimOffspring");var subQ8=sQuery(id+"F7.wireOp",EDGE,"E20");var subQ9=sQuery(id+"F7.wireOp",EDGE,"E15.trimOffspring");var subQ10=sQuery(id+"F7.wireOp",EDGE,"E18");var subQ11=sQuery(id+"F7.wireOp",EDGE,"E23");var subQ12=sQuery(id+"F7.wireOp",EDGE,"E13.right");var subQ17=sQuery(id+"F7.wireOp",EDGE,"E16");var subQ18=sQuery(id+"F7.wireOp",EDGE,"E12.bottom");var subQ19=sQuery(id+"F7.wireOp",EDGE,"E21");var subQ22=sQuery(id+"F7.wireOp",EDGE,"E22");var subQ23=sQuery(id+"F7.wireOp",EDGE,"E19");var subQ24=sQuery(id+"F7.wireOp",EDGE,"E12.left");Q0=makeQuery(id+"F17.opExtrude","CAP_FACE",FACE,{"disambiguationData":[OSD([subQ5,subQ6,subQ4,subQ18,subQ1,subQ24,subQ3,subQ12,subQ7,subQ9,subQ17,subQ0,subQ10,subQ23,subQ8,subQ19,subQ22,subQ11]),TDD([makeQuery(id+"F16.boolean.opBoolean","SPLIT",FACE,{"disambiguationData":[TD([makeQuery(id+"F16.opExtrude","SWEPT_FACE",FACE,{"disambiguationData":[OSD([sQuery(id+"F15.wireOp",EDGE,"E26")])]})])],"derivedFrom":makeQuery(id+"F13.boolean.opBoolean","SPLIT",FACE,{"disambiguationData":[TD([makeQuery(id+"F8.boolean.opBoolean","COPY",FACE,{"derivedFrom":makeQuery(id+"F8.opExtrude","SWEPT_FACE",FACE,{"disambiguationData":[OSD([subQ5])]})})])],"derivedFrom":makeQuery(id+"F8.boolean.opBoolean","COPY",FACE,{"derivedFrom":makeQuery(id+"F8.opExtrude","CAP_FACE",FACE,{"disambiguationData":[OSD([subQ5,subQ6,subQ4,subQ18,subQ1,subQ24,subQ3,subQ12,subQ7,subQ9,subQ17,subQ0,subQ10,subQ23,subQ8,subQ19,subQ22,subQ11])],"isStart":false})})})})])],"isStart":false});}
            var sketch = newSketch(context, id + "F53", { "sketchPlane" : qUnion([Q0])});
            skCircle(sketch, "E76", {"center": v(4.93, -2.43) * mm, "radius": 0.64 * mm});
            skSolve(sketch);
        }
        {
            var Q0;
            Q0=makeQuery(id+"F5.opExtrude","CAP_FACE",FACE,{"disambiguationData":[OSD([sQuery(id+"F4.wireOp",EDGE,"E8.bottom"),sQuery(id+"F4.wireOp",EDGE,"E8.top"),sQuery(id+"F4.wireOp",EDGE,"E8.left"),sQuery(id+"F4.wireOp",EDGE,"E8.right")])],"isStart":false});
            var sketch = newSketch(context, id + "F54", { "sketchPlane" : qUnion([Q0])});
            skCircle(sketch, "E77", {"center": v(18.38, 22.76) * mm, "radius": 0.64 * mm});
            skPoint(sketch, "E77.centerSnap0", {"position": v(13.93, 22.76) * mm});
            skPoint(sketch, "E77.centerSnap1", {"position": v(18.38, 29.1) * mm});
            skCircle(sketch, "E78", {"center": v(29.74, 22.76) * mm, "radius": 0.64 * mm});
            skPoint(sketch, "E78.centerSnap0", {"position": v(22.82, 22.76) * mm});
            skSolve(sketch);
        }
        {
            var Q0;
            Q0=makeQuery(id+"F53.imprint","IMPRINT",FACE,{"disambiguationData":[TD([[makeQuery(id+"F53.imprint","IMPRINT",EDGE,{"derivedFrom":sQuery(id+"F53.wireOp",EDGE,"E76")}),1.0]])]});
            var Q1;
            Q1=makeQuery(id+"F54.imprint","IMPRINT",FACE,{"disambiguationData":[TD([[makeQuery(id+"F54.imprint","IMPRINT",EDGE,{"derivedFrom":sQuery(id+"F54.wireOp",EDGE,"E77")}),1.0]])]});
            var Q2;
            Q2=makeQuery(id+"F54.imprint","IMPRINT",FACE,{"disambiguationData":[TD([[makeQuery(id+"F54.imprint","IMPRINT",EDGE,{"derivedFrom":sQuery(id+"F54.wireOp",EDGE,"E78")}),1.0]])]});
            extrude(context, id + "F55", {"entities" : qUnion([Q0, Q1, Q2]), "operationType" : NewBodyOperationType.ADD, "depth" : 0.32 * mm});
        }
        {
            var Q0;
            Q0=makeQuery(id+"F55.opExtrude","CAP_EDGE",EDGE,{"disambiguationData":[OSD([sQuery(id+"F53.wireOp",EDGE,"E76")])],"isStart":false});
            var Q1;
            Q1=makeQuery(id+"F55.opExtrude","CAP_EDGE",EDGE,{"disambiguationData":[OSD([sQuery(id+"F54.wireOp",EDGE,"E77")])],"isStart":false});
            var Q2;
            Q2=makeQuery(id+"F55.opExtrude","CAP_EDGE",EDGE,{"disambiguationData":[OSD([sQuery(id+"F54.wireOp",EDGE,"E78")])],"isStart":false});
            fillet(context, id + "F56", {"entities" : qUnion([Q0, Q1, Q2]), "radius" : 0.32 * mm, "tangentPropagation" : true, "allowEdgeOverflow" : false});
        }
        {
            var Q0;
            {var subQ2=sQuery(id+"F0.wireOp",EDGE,"E0.top");var subQ4=sQuery(id+"F0.wireOp",EDGE,"E0.right");var subQ5=sQuery(id+"F24.wireOp",EDGE,"E44");var subQ7=makeQuery(id+"F1.opExtrude","CAP_FACE",FACE,{"disambiguationData":[OSD([subQ2,sQuery(id+"F0.wireOp",EDGE,"E0.left"),subQ4,sQuery(id+"F0.wireOp",EDGE,"E1"),sQuery(id+"F0.wireOp",EDGE,"E3.bottom")])],"isStart":true});Q0=makeQuery(id+"F25.boolean.opBoolean","SPLIT",FACE,{"disambiguationData":[TD([makeQuery(id+"F25.opExtrude","SWEPT_FACE",FACE,{"disambiguationData":[OSD([subQ5])]})])],"derivedFrom":subQ7});}
            var sketch = newSketch(context, id + "F57", { "sketchPlane" : qUnion([Q0])});
            skLineSegment(sketch, "E79.bottom", {"start": v(0, -9) * mm, "end": v(10.16, -9) * mm});
            skLineSegment(sketch, "E79.top", {"start": v(0, -7.73) * mm, "end": v(10.16, -7.73) * mm});
            skLineSegment(sketch, "E79.left", {"start": v(0, -9) * mm, "end": v(0, -7.73) * mm});
            skLineSegment(sketch, "E79.right", {"start": v(10.16, -9) * mm, "end": v(10.16, -7.73) * mm});
            skLineSegment(sketch, "E80.bottom", {"start": v(0, -5.2) * mm, "end": v(10.16, -5.2) * mm});
            skLineSegment(sketch, "E80.top", {"start": v(0, -3.92) * mm, "end": v(10.16, -3.92) * mm});
            skLineSegment(sketch, "E80.left", {"start": v(0, -5.2) * mm, "end": v(0, -3.92) * mm});
            skLineSegment(sketch, "E80.right", {"start": v(10.16, -5.2) * mm, "end": v(10.16, -3.92) * mm});
            skLineSegment(sketch, "E81.bottom", {"start": v(0, -1.38) * mm, "end": v(10.16, -1.38) * mm});
            skLineSegment(sketch, "E81.top", {"start": v(0, -0.11) * mm, "end": v(10.16, -0.11) * mm});
            skLineSegment(sketch, "E81.left", {"start": v(0, -1.38) * mm, "end": v(0, -0.11) * mm});
            skLineSegment(sketch, "E81.right", {"start": v(10.16, -1.38) * mm, "end": v(10.16, -0.11) * mm});
            skLineSegment(sketch, "E82.bottom", {"start": v(0, 2.43) * mm, "end": v(10.16, 2.43) * mm});
            skLineSegment(sketch, "E82.top", {"start": v(0, 3.7) * mm, "end": v(10.16, 3.7) * mm});
            skLineSegment(sketch, "E82.left", {"start": v(0, 2.43) * mm, "end": v(0, 3.7) * mm});
            skLineSegment(sketch, "E82.right", {"start": v(10.16, 2.43) * mm, "end": v(10.16, 3.7) * mm});
            skSolve(sketch);
        }
        {
            var Q0;
            Q0 = qSketchRegion(id + "F57", true);
            extrude(context, id + "F58", {"entities" : qUnion([Q0]), "operationType" : NewBodyOperationType.REMOVE, "oppositeDirection" : true, "depth" : 0.64 * mm});
        }
        {
            var Q0;
            Q0=makeQuery(id+"F5.opExtrude","CAP_FACE",FACE,{"disambiguationData":[OSD([sQuery(id+"F4.wireOp",EDGE,"E6.bottom"),sQuery(id+"F4.wireOp",EDGE,"E6.top"),sQuery(id+"F4.wireOp",EDGE,"E6.left"),sQuery(id+"F4.wireOp",EDGE,"E6.right")])],"isStart":false});
            var sketch = newSketch(context, id + "F59", { "sketchPlane" : qUnion([Q0])});
            skArc(sketch, "E83", {"start": v(-25.52, 26.29) * mm, "mid": v(-23.96, 17.69) * mm, "end": v(-22.4, 26.29) * mm});
            skFitSpline(sketch, "E84", {"points": [v(-25.52, 26.29) * mm, v(-23.96, 22.13) * mm], "startDerivative": vector(-7.16, -6.38) * mm, "endDerivative": vector(8.24, 4.96) * mm});
            skFitSpline(sketch, "E85", {"points": [v(-22.4, 26.29) * mm, v(-23.96, 22.13) * mm], "startDerivative": vector(7.16, -6.38) * mm, "endDerivative": vector(-8.8, 4.96) * mm});
            skFitSpline(sketch, "E86", {"points": [v(-24.97, 21.74) * mm, v(-25.13, 24.9) * mm], "startDerivative": vector(4.12, 2.7) * mm, "endDerivative": vector(0.39, -0.5) * mm});
            skFitSpline(sketch, "E87", {"points": [v(-22.9, 21.74) * mm, v(-22.87, 24.9) * mm], "startDerivative": vector(-4.23, 2.7) * mm, "endDerivative": vector(-0.4, -0.5) * mm});
            skLineSegment(sketch, "E88", {"start": v(-25.13, 24.9) * mm, "end": v(-24.72, 25.31) * mm});
            skLineSegment(sketch, "E89", {"start": v(-25.7, 24.9) * mm, "end": v(-24.28, 24.9) * mm, "construction": true});
            skLineSegment(sketch, "E90", {"start": v(-22.87, 24.9) * mm, "end": v(-23.28, 25.31) * mm});
            skFitSpline(sketch, "E91", {"points": [v(-24.72, 25.31) * mm, v(-24.32, 24.76) * mm], "startDerivative": vector(0.46, -0.42) * mm, "endDerivative": vector(0.3, -0.74) * mm});
            skFitSpline(sketch, "E92", {"points": [v(-23.28, 25.31) * mm, v(-23.6, 24.76) * mm], "startDerivative": vector(-0.45, -0.43) * mm, "endDerivative": vector(-0.16, -0.69) * mm});
            skFitSpline(sketch, "E93", {"points": [v(-24.32, 24.76) * mm, v(-24.46, 25.57) * mm], "startDerivative": vector(0.06, 0.73) * mm, "endDerivative": vector(-0.42, 0.7) * mm});
            skFitSpline(sketch, "E94", {"points": [v(-23.6, 24.76) * mm, v(-23.54, 25.57) * mm], "startDerivative": vector(-0.14, 0.73) * mm, "endDerivative": vector(0.3, 0.7) * mm});
            skLineSegment(sketch, "E95", {"start": v(-24.46, 25.57) * mm, "end": v(-23.96, 26.33) * mm});
            skLineSegment(sketch, "E96", {"start": v(-23.96, 26.33) * mm, "end": v(-23.54, 25.57) * mm});
            skSolve(sketch);
        }
        {
            var Q0;
            Q0 = qSketchRegion(id + "F59", true);
            extrude(context, id + "F60", {"entities" : qUnion([Q0]), "operationType" : NewBodyOperationType.REMOVE, "oppositeDirection" : true, "depth" : 0.64 * mm});
        }
    });
